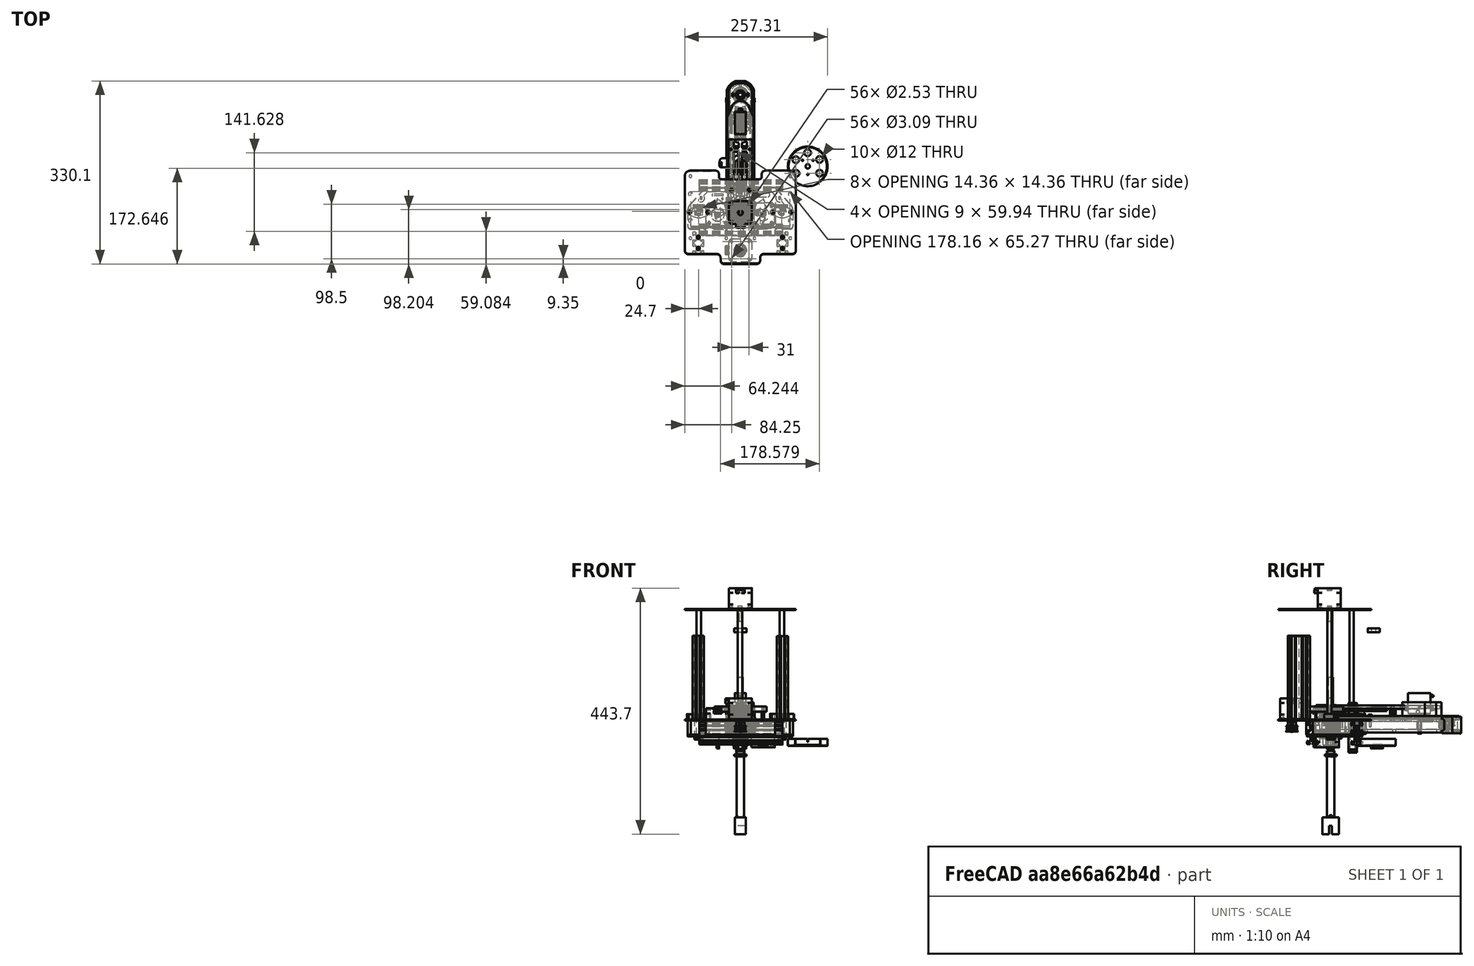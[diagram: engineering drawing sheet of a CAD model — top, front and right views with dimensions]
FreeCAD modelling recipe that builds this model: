
FCSTD DOCUMENT  (FreeCAD 1.0R38641 +468 (Git))
Label: zaxis
License: All rights reserved
LicenseURL: https://en.wikipedia.org/wiki/All_rights_reserved
objects: Part::Feature×117, Sketcher::SketchObject×42, App::Part×40, PartDesign::Body×25, PartDesign::Pad×24, PartDesign::Pocket×13, Mesh::Feature×12, TechDraw::DrawSVGTemplate×4, TechDraw::DrawPage×4, PartDesign::FeatureBase×2, PartDesign::Fillet×2, PartDesign::PolarPattern×1
note: 349 computed .brp shape members not serialized (recipe doc carries the construction recipe); baked Part::Feature solids carry a one-line shape summary decoded from their .brp

FEATURE [Sketcher::SketchObject] Sketch
  ArcFitTolerance = 1e-06
  AttachmentSupport = -> [XY_Plane001]
  FullyConstrained = false
  MakeInternals = false
  MapMode = 5
  sketch-geometry (70):
    g0: LineSegment StartX=-100 StartY=65.5055 StartZ=0 EndX=-100 EndY=-68.9082 EndZ=0
    g1: LineSegment StartX=100 StartY=-68.9082 StartZ=0 EndX=100 EndY=64.34 EndZ=0
    g2: GeomPoint [constr] X=0 Y=0 Z=0
    g3: LineSegment StartX=-93.9082 StartY=-75 StartZ=0 EndX=-42.611 EndY=-75 EndZ=0
    g4: LineSegment StartX=93.9082 StartY=-75 StartZ=0 EndX=42.611 EndY=-75 EndZ=0
    g5: LineSegment StartX=-35.5796 StartY=-82.0314 StartZ=0 EndX=-35.5796 EndY=-86.8204 EndZ=0
    g6: LineSegment StartX=-30.0002 StartY=-92.3998 StartZ=0 EndX=30.0002 EndY=-92.3998 EndZ=0
    g7: LineSegment StartX=35.5796 StartY=-86.8204 StartZ=0 EndX=35.5796 EndY=-82.0314 EndZ=0
    g8: LineSegment [constr] StartX=-127.885 StartY=50 StartZ=0 EndX=133.274 EndY=50 EndZ=0
    g9: LineSegment [constr] StartX=-138.289 StartY=-30 StartZ=0 EndX=153.891 EndY=-30 EndZ=0
    g10: LineSegment [constr] StartX=80 StartY=84.0683 StartZ=0 EndX=80 EndY=-102.927 EndZ=0
    g11: LineSegment [constr] StartX=-80 StartY=84.0683 StartZ=0 EndX=-80 EndY=-111.043 EndZ=0
    g12: ArcOfCircle CenterX=-93.9082 CenterY=-68.9082 CenterZ=0 NormalX=0 NormalY=0 NormalZ=1 AngleXU=0 Radius=6.09183 StartAngle=3.14159 EndAngle=4.71239
    g13: GeomPoint [constr] X=-100 Y=-75 Z=0
    g14: ArcOfCircle CenterX=-30.0002 CenterY=-86.8204 CenterZ=0 NormalX=0 NormalY=0 NormalZ=1 AngleXU=0 Radius=5.57938 StartAngle=3.14159 EndAngle=4.71239
    g15: GeomPoint [constr] X=-35.5796 Y=-92.3998 Z=0
    g16: ArcOfCircle CenterX=30.0002 CenterY=-86.8204 CenterZ=0 NormalX=0 NormalY=0 NormalZ=1 AngleXU=0 Radius=5.57938 StartAngle=4.71239 EndAngle=6.28319
    g17: GeomPoint [constr] X=35.5796 Y=-92.3998 Z=0
    g18: ArcOfCircle CenterX=-42.611 CenterY=-82.0314 CenterZ=0 NormalX=0 NormalY=0 NormalZ=1 AngleXU=0 Radius=7.03144 StartAngle=6e-16 EndAngle=1.5708
    g19: GeomPoint [constr] X=-35.5796 Y=-75 Z=0
    g20: ArcOfCircle CenterX=42.611 CenterY=-82.0314 CenterZ=0 NormalX=0 NormalY=0 NormalZ=1 AngleXU=0 Radius=7.03144 StartAngle=1.5708 EndAngle=3.14159
    g21: GeomPoint [constr] X=35.5796 Y=-75 Z=0
    g22: ArcOfCircle CenterX=93.9082 CenterY=-68.9082 CenterZ=0 NormalX=0 NormalY=0 NormalZ=1 AngleXU=0 Radius=6.09183 StartAngle=4.71239 EndAngle=6.28319
    g23: GeomPoint [constr] X=100 Y=-75 Z=0
    g24: LineSegment [constr] StartX=90 StartY=-14.05 StartZ=0 EndX=-90 EndY=-14.05 EndZ=0
    g25: LineSegment [constr] StartX=-90 StartY=-14.05 StartZ=0 EndX=-90 EndY=-45.95 EndZ=0
    g26: LineSegment [constr] StartX=-90 StartY=-45.95 StartZ=0 EndX=90 EndY=-45.95 EndZ=0
    g27: LineSegment [constr] StartX=90 StartY=-45.95 StartZ=0 EndX=90 EndY=-14.05 EndZ=0
    g28: LineSegment [constr] StartX=-90 StartY=65.95 StartZ=0 EndX=-90 EndY=34.05 EndZ=0
    g29: LineSegment [constr] StartX=-90 StartY=34.05 StartZ=0 EndX=90 EndY=34.05 EndZ=0
    g30: LineSegment [constr] StartX=90 StartY=34.05 StartZ=0 EndX=90 EndY=65.95 EndZ=0
    g31: LineSegment [constr] StartX=90 StartY=65.95 StartZ=0 EndX=-90 EndY=65.95 EndZ=0
    g32: Circle CenterX=90 CenterY=65.95 CenterZ=0 NormalX=0 NormalY=0 NormalZ=1 AngleXU=0 Radius=2.5
    g33: Circle CenterX=-90 CenterY=65.95 CenterZ=0 NormalX=0 NormalY=0 NormalZ=1 AngleXU=0 Radius=2.5
    g34: Circle CenterX=-90 CenterY=-45.95 CenterZ=0 NormalX=0 NormalY=0 NormalZ=1 AngleXU=0 Radius=2.5
    g35: Circle CenterX=90 CenterY=-45.95 CenterZ=0 NormalX=0 NormalY=0 NormalZ=1 AngleXU=0 Radius=2.5
    g36: LineSegment [constr] StartX=-76 StartY=-45 StartZ=0 EndX=-76 EndY=-65 EndZ=0
    g37: LineSegment [constr] StartX=-76 StartY=-65 StartZ=0 EndX=76 EndY=-65 EndZ=0
    g38: LineSegment [constr] StartX=76 StartY=-65 StartZ=0 EndX=76 EndY=-45 EndZ=0
    g39: LineSegment [constr] StartX=76 StartY=-45 StartZ=0 EndX=-76 EndY=-45 EndZ=0
    g40: GeomPoint [constr] X=-157.396 Y=0 Z=0
    g41: GeomPoint [constr] X=-25.3688 Y=-45.95 Z=0
    g42: GeomPoint [constr] X=25.3688 Y=-45.95 Z=0
    g43: Circle CenterX=-25.3688 CenterY=-45.95 CenterZ=0 NormalX=0 NormalY=0 NormalZ=1 AngleXU=0 Radius=2.5
    g44: Circle CenterX=25.3688 CenterY=-45.95 CenterZ=0 NormalX=0 NormalY=0 NormalZ=1 AngleXU=0 Radius=2.5
    g45: Circle CenterX=-90 CenterY=34.05 CenterZ=0 NormalX=0 NormalY=0 NormalZ=1 AngleXU=0 Radius=3.58
    g46: Circle CenterX=-90 CenterY=-14.05 CenterZ=0 NormalX=0 NormalY=0 NormalZ=1 AngleXU=0 Radius=3.58
    g47: Circle CenterX=90 CenterY=34.05 CenterZ=0 NormalX=0 NormalY=0 NormalZ=1 AngleXU=0 Radius=3.58
    g48: Circle CenterX=90 CenterY=-14.05 CenterZ=0 NormalX=0 NormalY=0 NormalZ=1 AngleXU=0 Radius=3.58
    g49: Circle CenterX=-76 CenterY=-65 CenterZ=0 NormalX=0 NormalY=0 NormalZ=1 AngleXU=0 Radius=2.7
    g50: Circle CenterX=-76 CenterY=-45 CenterZ=0 NormalX=0 NormalY=0 NormalZ=1 AngleXU=0 Radius=2.7
    g51: Circle CenterX=76 CenterY=-65 CenterZ=0 NormalX=0 NormalY=0 NormalZ=1 AngleXU=0 Radius=2.7
    g52: Circle CenterX=76 CenterY=-45 CenterZ=0 NormalX=0 NormalY=0 NormalZ=1 AngleXU=0 Radius=2.7
    g53: ArcOfCircle CenterX=89.2751 CenterY=64.34 CenterZ=0 NormalX=0 NormalY=0 NormalZ=1 AngleXU=0 Radius=10.7249 StartAngle=0 EndAngle=1.56696
    g54: GeomPoint [constr] X=100 Y=75 Z=0
    g55: ArcOfCircle CenterX=-90.4406 CenterY=65.5055 CenterZ=0 NormalX=0 NormalY=0 NormalZ=1 AngleXU=0 Radius=9.55939 StartAngle=1.5752 EndAngle=3.14159
    g56: GeomPoint [constr] X=-100 Y=75 Z=0
    g57: LineSegment StartX=-90.4827 StartY=75.0648 StartZ=0 EndX=-44.8342 EndY=75.0648 EndZ=0
    g58: LineSegment StartX=89.3163 StartY=75.0648 StartZ=0 EndX=44.8342 EndY=75.0648 EndZ=0
    g59: LineSegment StartX=38.4638 StartY=68.6944 StartZ=0 EndX=38.4638 EndY=63.8553 EndZ=0
    g60: LineSegment StartX=34.2439 StartY=59.6354 StartZ=0 EndX=-34.2439 EndY=59.6354 EndZ=0
    g61: LineSegment StartX=-38.4638 StartY=63.8553 StartZ=0 EndX=-38.4638 EndY=68.6944 EndZ=0
    g62: ArcOfCircle CenterX=-44.8342 CenterY=68.6944 CenterZ=0 NormalX=0 NormalY=0 NormalZ=1 AngleXU=0 Radius=6.37042 StartAngle=-9e-16 EndAngle=1.5708
    g63: GeomPoint [constr] X=-38.4638 Y=75.0648 Z=0
    g64: ArcOfCircle CenterX=44.8342 CenterY=68.6944 CenterZ=0 NormalX=0 NormalY=0 NormalZ=1 AngleXU=0 Radius=6.37042 StartAngle=1.5708 EndAngle=3.14159
    g65: GeomPoint [constr] X=38.4638 Y=75.0648 Z=0
    g66: ArcOfCircle CenterX=34.2439 CenterY=63.8553 CenterZ=0 NormalX=0 NormalY=0 NormalZ=1 AngleXU=0 Radius=4.21993 StartAngle=4.71239 EndAngle=6.28319
    g67: GeomPoint [constr] X=38.4638 Y=59.6354 Z=0
    g68: ArcOfCircle CenterX=-34.2439 CenterY=63.8553 CenterZ=0 NormalX=0 NormalY=0 NormalZ=1 AngleXU=0 Radius=4.21993 StartAngle=3.14159 EndAngle=4.71239
    g69: GeomPoint [constr] X=-38.4638 Y=59.6354 Z=0
  constraints (137):
    c: Vertical(g0)
    c: Vertical(g1)
    c: Horizontal(g3)
    c: Horizontal(g4)
    c: Vertical(g5)
    c: Horizontal(g6)
    c: Vertical(g7)
    c: Symmetric(g19,g21,g-2)
    c: Horizontal(g8)
    c: Horizontal(g9)
    c: DistanceY(g9,g8) = 80
    c: Vertical(g10)
    c: Vertical(g11)
    c: Symmetric(g11,g10,g-2)
    c: DistanceX(g13,g11) = 20
    c: DistanceX(g11,g10) = 160
    c: PointOnObject(g13,g0)
    c: PointOnObject(g13,g3)
    c: Tangent(g0,g12) = -1.5708
    c: Tangent(g3,g12) = -1.5708
    c: PointOnObject(g15,g5)
    c: PointOnObject(g15,g6)
    c: Tangent(g5,g14) = -1.5708
    c: Tangent(g6,g14) = -1.5708
    c: PointOnObject(g17,g6)
    c: PointOnObject(g17,g7)
    c: Tangent(g6,g16) = -1.5708
    c: Tangent(g7,g16) = -1.5708
    c: PointOnObject(g19,g3)
    c: PointOnObject(g19,g5)
    c: Tangent(g3,g18) = 1.5708
    c: Tangent(g5,g18) = 1.5708
    c: PointOnObject(g21,g4)
    c: PointOnObject(g21,g7)
    c: Tangent(g4,g20) = -1.5708
    c: Tangent(g7,g20) = 1.5708
    c: PointOnObject(g23,g1)
    c: PointOnObject(g23,g4)
    c: Tangent(g1,g22) = -1.5708
    c: Tangent(g4,g22) = 1.5708
    c: Horizontal(g12,g22)
    c: Coincident(g24,g25)
    c: Coincident(g25,g26)
    c: Coincident(g26,g27)
    c: Coincident(g27,g24)
    c: Horizontal(g24)
    c: Horizontal(g26)
    c: Vertical(g25)
    c: DistanceY(g26,g24) = 31.9
    c: Symmetric(g26,g24,g9)
    c: Coincident(g28,g29)
    c: Coincident(g29,g30)
    c: Coincident(g30,g31)
    c: Coincident(g31,g28)
    c: Vertical(g28)
    c: Horizontal(g29)
    c: Horizontal(g31)
    c: DistanceY(g29,g30) = 31.9
    c: Symmetric(g29,g30,g8)
    c: Vertical(g24,g29)
    c: Vertical(g28,g24)
    c: DistanceX(g56,g28) = 10
    c: DistanceX(g30,g54) = 10
    c: Coincident(g32,g30)
    c: Coincident(g33,g28)
    c: Coincident(g34,g25)
    c: Coincident(g35,g26)
    c: Equal(g35,g32)
    c: Equal(g35,g33)
    c: Equal(g35,g34)
    c: Coincident(g36,g37)
    c: Coincident(g37,g38)
    c: Coincident(g38,g39)
    c: Coincident(g39,g36)
    c: Vertical(g36)
    c: Vertical(g38)
    c: Horizontal(g39)
    c: DistanceY(g36,g36) = 20
    c: Symmetric(g36,g37,g-2)
    c: PointOnObject(g40,g-1)
    c: DistanceY(g36,g40) = 45
    c: DistanceX(g25,g36) = 14
    c: PointOnObject(g41,g26)
    c: Coincident(g43,g41)
    c: Coincident(g44,g42)
    c: Symmetric(g42,g41,g-2)
    c: Diameter(g34) = 5
    c: Diameter(g43) = 5
    c: Diameter(g44) = 5
    c: Coincident(g45,g28)
    c: Coincident(g46,g24)
    c: Coincident(g47,g29)
    c: Coincident(g48,g24)
    c: Equal(g47,g48)
    c: Equal(g47,g45)
    c: Equal(g47,g46)
    c: Diameter(g47) = 7.16
    c: Coincident(g49,g36)
    c: Coincident(g50,g36)
    c: Coincident(g51,g37)
    c: Coincident(g52,g38)
    c: Equal(g52,g51)
    c: Equal(g52,g49)
    c: Equal(g52,g50)
    c: Diameter(g52) = 5.4
    c: PointOnObject(g54,g1)
    c: Tangent(g1,g53) = -1.5708
    c: PointOnObject(g56,g0)
    c: Tangent(g0,g55) = -1.5708
    c: Coincident(g57,g55)
    c: Horizontal(g57)
    c: Coincident(g58,g53)
    c: Horizontal(g58)
    c: Vertical(g59)
    c: Horizontal(g60)
    c: Vertical(g61)
    c: Symmetric(g63,g65,g-2)
    c: PointOnObject(g63,g57)
    c: PointOnObject(g63,g61)
    c: Tangent(g57,g62) = 1.5708
    c: Tangent(g61,g62) = -1.5708
    c: PointOnObject(g65,g58)
    c: PointOnObject(g65,g59)
    c: Tangent(g58,g64) = -1.5708
    c: Tangent(g59,g64) = -1.5708
    c: PointOnObject(g67,g59)
    c: PointOnObject(g67,g60)
    c: Tangent(g59,g66) = 1.5708
    c: Tangent(g60,g66) = 1.5708
    c: PointOnObject(g69,g60)
    c: PointOnObject(g69,g61)
    c: Tangent(g60,g68) = 1.5708
    c: Tangent(g61,g68) = 1.5708
    c: Horizontal(g68,g66)
    c: Horizontal(g62,g64)
    c: Horizontal(g18,g20)
    c: Horizontal(g14,g16)
FEATURE [PartDesign::Pad] Pad
  Direction = (0,0,1)
  Length = 2
  Length2 = 10
  Profile = -> Sketch
  ReferenceAxis = -> Sketch [N_Axis]
  Refine = true
  Suppressed = false
  Type = 0
FEATURE [Mesh::Feature] Arm_Base_MotorPlate_1_1_003  label="Arm_Base_MotorPlate_1.1.003"
  Placement = pos=(0,0,113) rot=(0,0,1;0rad)
FEATURE [Mesh::Feature] Arm_Base_ZHub_Bottom_1_0_0  label="Arm_Base_ZHub_Bottom_1.0.0"
  Placement = pos=(25,30.5,141) rot=(0,0,1;3.14159rad)
FEATURE [Mesh::Feature] Arm_Base_ZHub_Top_1_0_0  label="Arm_Base_ZHub_Top_1.0.0"
  Placement = pos=(7.5,4.5e-15,112.5) rot=(1,0,0;3.14159rad)
FEATURE [Mesh::Feature] Arm_Shoulder_Connector_1_1_2  label="Arm_Shoulder_Connector_1.1.2"
  Placement = pos=(-3.6e-15,38,156) rot=(1,0,0;1.5708rad)
FEATURE [Mesh::Feature] Arm_Shoulder_Connector_1_1_003  label="Arm_Shoulder_Connector_1.1.003"
  Placement = pos=(0,38,85.5) rot=(1,0,0;1.5708rad)
FEATURE [Mesh::Feature] GT2_20_T_5mm_bore  label="GT2 20 T 5mm bore"
  Placement = pos=(-44,6,159) rot=(1,0,0;3.14159rad)
FEATURE [Mesh::Feature] GT2_20_T_5mm_bore001  label="GT2 20 T 5mm bore001"
  Placement = pos=(44,5.5,92) rot=(0,0,1;3.14159rad)
FEATURE [Part::Feature] Part__Feature003  label="LM8LUU Long Type Linear Bearing"
  Placement = pos=(-1.63e-14,39.5,31.8) rot=(0,1,0;1.5708rad)
  shape: bbox 15 x 15 x 45 mm, 34 faces (baked)
FEATURE [Part::Feature] Part__Feature005  label="LM8LUU Long Type Linear Bearing001"
  Placement = pos=(-6.4e-15,39.5,-12.8) rot=(0,1,0;1.5708rad)
  shape: bbox 15 x 15 x 45 mm, 34 faces (baked)
FEATURE [Part::Feature] Part__Feature008  label="p  BEARING, METRIC 600 MINIATURE SERIES, DOUBLE-SEALED  8mm ID × 22 OD × 7 W  —  608-2RS"
  Placement = pos=(-0.5,83.3,-46.6) rot=(0,0,1;0rad)
  shape: bbox 23.81 x 23.81 x 7.015 mm, 606 faces (baked)
FEATURE [Part::Feature] Part__Feature009  label="p  BEARING, METRIC 600 MINIATURE SERIES, DOUBLE-SEALED  8mm ID × 22 OD × 7 W  —  608-2RS001"
  Placement = pos=(0,77.5,163) rot=(0,0,1;0rad)
  shape: bbox 23.81 x 23.81 x 7.015 mm, 606 faces (baked)
FEATURE [Part::Feature] Part__Feature010  label="bearing"
  shape: bbox 8.659 x 4.3 x 8.659 mm, 17 faces (baked)
FEATURE [Part::Feature] Part__Feature011  label="bearing001"
  shape: bbox 8.659 x 4.3 x 8.659 mm, 17 faces (baked)
FEATURE [App::Part] bearing  label="bearing002"
  Group = -> [Part__Feature010,Part__Feature011]
  Origin = -> Origin005
FEATURE [Part::Feature] Part__Feature012  label="outer_plate"
  shape: bbox 12.9 x 8.6 x 12.9 mm, 12 faces (baked)
FEATURE [App::Part] GT2_Pulley_3mm_bore_v8  label="GT2 Pulley 3mm bore v8"
  Group = -> [bearing,Part__Feature012]
  Origin = -> Origin006
  Placement = pos=(44.8,29.9,9.8) rot=(1,0,0;1.5708rad)
FEATURE [Part::Feature] Part__Feature013  label="p  BEARING, SINGLE-ROW RADIAL, DOUBLE-SHIELDED, METRIC 6000-ZZ SERIES  —  6002-ZZ — 15mm ID × 32mm OD × 9mm W"
  shape: bbox 19.25 x 19.25 x 9 mm, 14 faces (baked)
FEATURE [Part::Feature] Part__Feature015  label="p  BEARING, SINGLE-ROW RADIAL, DOUBLE-SHIELDED, METRIC 6000-ZZ SERIES  —  6002-ZZ — 15mm ID × 32mm OD × 9mm W002"
  shape: bbox 29.3 x 29.3 x 8.937 mm, 1151 faces (baked)
FEATURE [Part::Feature] Part__Feature014  label="p  BEARING, SINGLE-ROW RADIAL, DOUBLE-SHIELDED, METRIC 6000-ZZ SERIES  —  6002-ZZ — 15mm ID × 32mm OD × 9mm W001"
  shape: bbox 34.64 x 34.64 x 9 mm, 14 faces (baked)
FEATURE [App::Part] p__BEARING__SINGLE_ROW_RADIAL__DOUBLE_SHIELDED__METRIC_6000_ZZ_SERIES_______6002_ZZ_____15mm_ID____32mm_OD____9mm_W  label="p  BEARING, SINGLE-ROW RADIAL, DOUBLE-SHIELDED, METRIC 6000-ZZ SERIES  —  6002-ZZ — 15mm ID × 32mm OD × 9mm W003"
  Group = -> [Part__Feature013,Part__Feature014,Part__Feature015]
  Origin = -> Origin007
  Placement = pos=(0,39.5,-33.1) rot=(0,0,1;0rad)
FEATURE [Part::Feature] Part__Feature016  label="p  BEARING, SINGLE-ROW RADIAL, DOUBLE-SHIELDED, METRIC 6000-ZZ SERIES  —  6002-ZZ — 15mm ID × 32mm OD × 9mm W004"
  shape: bbox 19.25 x 19.25 x 9 mm, 14 faces (baked)
FEATURE [Part::Feature] Part__Feature017  label="p  BEARING, SINGLE-ROW RADIAL, DOUBLE-SHIELDED, METRIC 6000-ZZ SERIES  —  6002-ZZ — 15mm ID × 32mm OD × 9mm W005"
  shape: bbox 34.64 x 34.64 x 9 mm, 14 faces (baked)
FEATURE [Part::Feature] Part__Feature018  label="p  BEARING, SINGLE-ROW RADIAL, DOUBLE-SHIELDED, METRIC 6000-ZZ SERIES  —  6002-ZZ — 15mm ID × 32mm OD × 9mm W006"
  shape: bbox 29.3 x 29.3 x 8.937 mm, 1151 faces (baked)
FEATURE [App::Part] p__BEARING__SINGLE_ROW_RADIAL__DOUBLE_SHIELDED__METRIC_6000_ZZ_SERIES_______6002_ZZ_____15mm_ID____32mm_OD____9mm_W001  label="p  BEARING, SINGLE-ROW RADIAL, DOUBLE-SHIELDED, METRIC 6000-ZZ SERIES  —  6002-ZZ — 15mm ID × 32mm OD × 9mm W007"
  Group = -> [Part__Feature016,Part__Feature017,Part__Feature018]
  Origin = -> Origin008
  Placement = pos=(0,39.5,9.5) rot=(0,0,1;0rad)
FEATURE [Part::Feature] Part__Feature019  label="KFL08Housing"
  shape: bbox 47 x 27 x 7.9 mm, 25 faces (baked)
FEATURE [Part::Feature] Part__Feature020  label="KFL08Bearing"
  shape: bbox 22 x 22 x 11.2 mm, 17 faces (baked)
FEATURE [Part::Feature] Part__Feature021  label="DIN_916-M3x3"
  Placement = pos=(0,-3.1,9.2) rot=(0,0,1;0rad)
  shape: bbox 3 x 3 x 3 mm, 11 faces (baked)
FEATURE [Part::Feature] Part__Feature022  label="DIN_916-M3x004"
  Placement = pos=(3.1,1.0252e-06,9.2) rot=(0,0,1;1.5708rad)
  shape: bbox 3 x 3 x 3 mm, 11 faces (baked)
FEATURE [App::Part] KFL08_Part  label="KFL08-Part"
  Group = -> [Part__Feature019,Part__Feature020,Part__Feature021,Part__Feature022]
  Origin = -> Origin009
  Placement = pos=(0,-2.5,2) rot=(0,0,1;0rad)
FEATURE [Part::Feature] Part__Feature024  label="Nema 17 model v004"
  Placement = pos=(1.48e-14,-70.5,40) rot=(0.707107,-0.707107,0;3.14159rad)
  shape: bbox 47.8 x 41.5 x 59.9 mm, 215 faces (baked)
FEATURE [Part::Feature] Part__Feature025  label="shf8mm"
  Placement = pos=(75,-2,2.5) rot=(0,0,1;3.14159rad)
  shape: bbox 43 x 24 x 10 mm, 66 faces (baked)
FEATURE [Part::Feature] Part__Feature026  label="Профиль V-slot 20x40"
  Placement = pos=(76,-33,-12.5) rot=(0.57735,-0.57735,-0.57735;2.0944rad)
  shape: bbox 150 x 20 x 40 mm, 80 faces (baked)
FEATURE [Part::Feature] Part__Feature027  label="Профиль V-slot 20x041"
  Placement = pos=(76,47,-13) rot=(0.57735,-0.57735,-0.57735;2.0944rad)
  shape: bbox 150 x 20 x 40 mm, 80 faces (baked)
FEATURE [Part::Feature] Part__Feature028  label="Профиль V-slot 20x042"
  Placement = pos=(76,-47.5,2.5) rot=(0,0,1;0rad)
  shape: bbox 20 x 40 x 150 mm, 80 faces (baked)
FEATURE [Part::Feature] Part__Feature029  label="Профиль V-slot 20x043"
  Placement = pos=(-76,-47.5,3) rot=(0,0,1;0rad)
  shape: bbox 20 x 40 x 150 mm, 80 faces (baked)
FEATURE [App::Part] Part003  label="RAIL"
  Group = -> [Part__Feature026,Part__Feature027]
  Origin = -> Origin011
  Placement = pos=(0,0,-2) rot=(0,0,1;0rad)
FEATURE [Sketcher::SketchObject] Sketch001
  ArcFitTolerance = 1e-06
  AttachmentSupport = -> [XY_Plane013]
  FullyConstrained = true
  MakeInternals = false
  MapMode = 5
  sketch-geometry (1):
    g0: Circle CenterX=0 CenterY=0 CenterZ=0 NormalX=0 NormalY=0 NormalZ=1 AngleXU=0 Radius=4
  constraints (2):
    c: Diameter(g0) = 8
    c: Coincident(g-1,g0)
FEATURE [PartDesign::Pad] Pad001
  Direction = (0,0,1)
  Length = 200
  Length2 = 10
  Profile = -> Sketch001
  ReferenceAxis = -> Sketch001 [N_Axis]
  Refine = true
  Suppressed = false
  Type = 0
FEATURE [PartDesign::Body] Body002  label="rod 8mm"
  AllowCompound = false
  Group = -> [Sketch001,Pad001]
  Origin = -> Origin013
  Placement = pos=(75,-2.5,0) rot=(0,0,1;0rad)
  Tip = -> Pad001
FEATURE [Sketcher::SketchObject] Sketch002
  ArcFitTolerance = 1e-06
  AttachmentSupport = -> [XY_Plane014]
  FullyConstrained = true
  MakeInternals = false
  MapMode = 5
  sketch-geometry (1):
    g0: Circle CenterX=0 CenterY=0 CenterZ=0 NormalX=0 NormalY=0 NormalZ=1 AngleXU=0 Radius=4
  constraints (2):
    c: Diameter(g0) = 8
    c: Coincident(g-1,g0)
FEATURE [PartDesign::Pad] Pad002
  Direction = (0,0,1)
  Length = 200
  Length2 = 10
  Profile = -> Sketch002
  ReferenceAxis = -> Sketch002 [N_Axis]
  Refine = true
  Suppressed = false
  Type = 0
FEATURE [PartDesign::Body] Body003  label="rod 8mm001"
  AllowCompound = false
  Group = -> [Sketch002,Pad002]
  Origin = -> Origin014
  Placement = pos=(-75,-1.5,0) rot=(0,0,1;0rad)
  Tip = -> Pad002
FEATURE [Sketcher::SketchObject] Sketch003
  ArcFitTolerance = 1e-06
  AttachmentSupport = -> [XY_Plane015]
  FullyConstrained = true
  MakeInternals = false
  MapMode = 5
  sketch-geometry (1):
    g0: Circle CenterX=0 CenterY=0 CenterZ=0 NormalX=0 NormalY=0 NormalZ=1 AngleXU=0 Radius=4
  constraints (2):
    c: Diameter(g0) = 8
    c: Coincident(g-1,g0)
FEATURE [PartDesign::Pad] Pad003
  Direction = (0,0,1)
  Length = 200
  Length2 = 10
  Profile = -> Sketch003
  ReferenceAxis = -> Sketch003 [N_Axis]
  Refine = true
  Suppressed = false
  Type = 0
FEATURE [PartDesign::Body] Body004  label="rod 8mm002"
  AllowCompound = false
  Group = -> [Sketch003,Pad003]
  Origin = -> Origin015
  Placement = pos=(-0.5,37.5,0) rot=(0,0,1;0rad)
  Tip = -> Pad003
FEATURE [Sketcher::SketchObject] Sketch005
  ArcFitTolerance = 1e-06
  AttachmentSupport = -> [XY_Plane017]
  FullyConstrained = true
  MakeInternals = false
  MapMode = 5
  sketch-geometry (1):
    g0: Circle CenterX=0 CenterY=0 CenterZ=0 NormalX=0 NormalY=0 NormalZ=1 AngleXU=0 Radius=3
  constraints (2):
    c: Coincident(g0,g-1)
    c: Diameter(g0) = 6
FEATURE [PartDesign::Body] Body006  label="fastener001"
  AllowCompound = false
  Group = -> [Sketch005]
  Origin = -> Origin017
  Placement = pos=(91.5,-48,-10) rot=(0,0,1;0rad)
FEATURE [Part::Feature] Part__Feature032  label="GT2_30T_5_6"
  Placement = pos=(-2.4e-15,-70,-2) rot=(0,1,0;3.14159rad)
  shape: bbox 23.27 x 23.27 x 17.5 mm, 336 faces (baked)
FEATURE [Part::Feature] Part__Feature033  label="15mm-wheel v003"
  Placement = pos=(0,-3.2e-15,-14.5) rot=(1,0,0;4.71239rad)
  shape: bbox 15.23 x 15.23 x 8.8 mm, 6 faces (baked)
FEATURE [Sketcher::SketchObject] Sketch006
  ArcFitTolerance = 1e-06
  AttachmentSupport = -> [XY_Plane019]
  FullyConstrained = true
  MakeInternals = false
  MapMode = 5
  sketch-geometry (1):
    g0: Circle CenterX=0 CenterY=0 CenterZ=0 NormalX=0 NormalY=0 NormalZ=1 AngleXU=0 Radius=3
  constraints (2):
    c: Coincident(g0,g-1)
    c: Diameter(g0) = 6
FEATURE [PartDesign::Pad] Pad006
  Direction = (0,0,1)
  Length = 10
  Length2 = 10
  Profile = -> Sketch006
  ReferenceAxis = -> Sketch006 [N_Axis]
  Refine = true
  Suppressed = false
  Type = 0
FEATURE [PartDesign::Body] Body007  label="fastener002"
  AllowCompound = false
  Group = -> [Sketch006,Pad006]
  Origin = -> Origin019
  Placement = pos=(0,0,0) rot=(1,0,0;3.14159rad)
  Tip = -> Pad006
FEATURE [App::Part] Part005  label="WHEEL ASSY001"
  Group = -> [Part__Feature033,Body007]
  Origin = -> Origin020
  Placement = pos=(25.5,-48.5,0) rot=(0,0,1;0rad)
FEATURE [Part::Feature] Part__Feature034  label="15mm-wheel v004"
  Placement = pos=(0,-2e-16,-15.5) rot=(1,0,0;4.71239rad)
  shape: bbox 15.23 x 15.23 x 8.8 mm, 6 faces (baked)
FEATURE [Sketcher::SketchObject] Sketch007
  ArcFitTolerance = 1e-06
  AttachmentSupport = -> [XY_Plane021]
  FullyConstrained = true
  MakeInternals = false
  MapMode = 5
  sketch-geometry (1):
    g0: Circle CenterX=0 CenterY=0 CenterZ=0 NormalX=0 NormalY=0 NormalZ=1 AngleXU=0 Radius=3
  constraints (2):
    c: Coincident(g0,g-1)
    c: Diameter(g0) = 6
FEATURE [PartDesign::Pad] Pad007
  Direction = (0,0,1)
  Length = 10
  Length2 = 10
  Profile = -> Sketch007
  ReferenceAxis = -> Sketch007 [N_Axis]
  Refine = true
  Suppressed = false
  Type = 0
FEATURE [Part::Feature] Part__Feature035  label="15mm-wheel v005"
  Placement = pos=(0,-2e-16,-15.5) rot=(1,0,0;4.71239rad)
  shape: bbox 15.23 x 15.23 x 8.8 mm, 6 faces (baked)
FEATURE [Sketcher::SketchObject] Sketch008
  ArcFitTolerance = 1e-06
  AttachmentSupport = -> [XY_Plane023]
  FullyConstrained = true
  MakeInternals = false
  MapMode = 5
  sketch-geometry (1):
    g0: Circle CenterX=0 CenterY=0 CenterZ=0 NormalX=0 NormalY=0 NormalZ=1 AngleXU=0 Radius=3
  constraints (2):
    c: Coincident(g0,g-1)
    c: Diameter(g0) = 6
FEATURE [PartDesign::Pad] Pad008
  Direction = (0,0,1)
  Length = 10
  Length2 = 10
  Profile = -> Sketch008
  ReferenceAxis = -> Sketch008 [N_Axis]
  Refine = true
  Suppressed = false
  Type = 0
FEATURE [PartDesign::Body] Body009  label="fastener004"
  AllowCompound = false
  Group = -> [Sketch008,Pad008]
  Origin = -> Origin023
  Placement = pos=(0,0,-10) rot=(0,0,1;0rad)
  Tip = -> Pad008
FEATURE [App::Part] Part007  label="WHEEL ASSY003"
  Group = -> [Part__Feature035,Body009]
  Origin = -> Origin024
  Placement = pos=(-25,-49,1) rot=(0,0,1;0rad)
FEATURE [Part::Feature] Part__Feature036  label="15mm-wheel v006"
  Placement = pos=(0,-2e-16,-15.5) rot=(1,0,0;4.71239rad)
  shape: bbox 15.23 x 15.23 x 8.8 mm, 6 faces (baked)
FEATURE [Sketcher::SketchObject] Sketch009
  ArcFitTolerance = 1e-06
  AttachmentSupport = -> [XY_Plane025]
  FullyConstrained = true
  MakeInternals = false
  MapMode = 5
  sketch-geometry (1):
    g0: Circle CenterX=0 CenterY=0 CenterZ=0 NormalX=0 NormalY=0 NormalZ=1 AngleXU=0 Radius=3
  constraints (2):
    c: Coincident(g0,g-1)
    c: Diameter(g0) = 6
FEATURE [PartDesign::Pad] Pad009
  Direction = (0,0,1)
  Length = 10
  Length2 = 10
  Profile = -> Sketch009
  ReferenceAxis = -> Sketch009 [N_Axis]
  Refine = true
  Suppressed = false
  Type = 0
FEATURE [PartDesign::Body] Body010  label="fastener005"
  AllowCompound = false
  Group = -> [Sketch009,Pad009]
  Origin = -> Origin025
  Placement = pos=(0,0,-10) rot=(0,0,1;0rad)
  Tip = -> Pad009
FEATURE [App::Part] Part008  label="WHEEL ASSY004"
  Group = -> [Part__Feature036,Body010]
  Origin = -> Origin026
  Placement = pos=(-90,-48.5,1) rot=(0,0,1;0rad)
FEATURE [Part::Feature] Part__Feature037  label="15mm-wheel v007"
  Placement = pos=(0,-2e-16,-15.5) rot=(1,0,0;4.71239rad)
  shape: bbox 15.23 x 15.23 x 8.8 mm, 6 faces (baked)
FEATURE [Sketcher::SketchObject] Sketch010
  ArcFitTolerance = 1e-06
  AttachmentSupport = -> [XY_Plane027]
  FullyConstrained = true
  MakeInternals = false
  MapMode = 5
  sketch-geometry (1):
    g0: Circle CenterX=0 CenterY=0 CenterZ=0 NormalX=0 NormalY=0 NormalZ=1 AngleXU=0 Radius=3
  constraints (2):
    c: Coincident(g0,g-1)
    c: Diameter(g0) = 6
FEATURE [PartDesign::Pad] Pad010
  Direction = (0,0,1)
  Length = 10
  Length2 = 10
  Profile = -> Sketch010
  ReferenceAxis = -> Sketch010 [N_Axis]
  Refine = true
  Suppressed = false
  Type = 0
FEATURE [PartDesign::Body] Body011  label="fastener006"
  AllowCompound = false
  Group = -> [Sketch010,Pad010]
  Origin = -> Origin027
  Placement = pos=(0,0,-10) rot=(0,0,1;0rad)
  Tip = -> Pad010
FEATURE [App::Part] Part009  label="WHEEL ASSY005"
  Group = -> [Part__Feature037,Body011]
  Origin = -> Origin028
  Placement = pos=(-90,-16.5,1) rot=(0,0,1;0rad)
FEATURE [Part::Feature] Part__Feature039  label="15mm-wheel v009"
  Placement = pos=(0,-2e-16,-15.5) rot=(1,0,0;4.71239rad)
  shape: bbox 15.23 x 15.23 x 8.8 mm, 6 faces (baked)
FEATURE [Sketcher::SketchObject] Sketch012
  ArcFitTolerance = 1e-06
  AttachmentSupport = -> [XY_Plane031]
  FullyConstrained = true
  MakeInternals = false
  MapMode = 5
  sketch-geometry (1):
    g0: Circle CenterX=0 CenterY=0 CenterZ=0 NormalX=0 NormalY=0 NormalZ=1 AngleXU=0 Radius=3
  constraints (2):
    c: Coincident(g0,g-1)
    c: Diameter(g0) = 6
FEATURE [PartDesign::Pad] Pad012
  Direction = (0,0,1)
  Length = 10
  Length2 = 10
  Profile = -> Sketch012
  ReferenceAxis = -> Sketch012 [N_Axis]
  Refine = true
  Suppressed = false
  Type = 0
FEATURE [PartDesign::Body] Body013  label="fastener008"
  AllowCompound = false
  Group = -> [Sketch012,Pad012]
  Origin = -> Origin031
  Placement = pos=(0,0,-10) rot=(0,0,1;0rad)
  Tip = -> Pad012
FEATURE [App::Part] Part011  label="WHEEL ASSY007"
  Group = -> [Part__Feature039,Body013]
  Origin = -> Origin032
  Placement = pos=(-90,63.5,1) rot=(0,0,1;0rad)
FEATURE [Part::Feature] Part__Feature040  label="15mm-wheel v010"
  Placement = pos=(0,-2e-16,-15.5) rot=(1,0,0;4.71239rad)
  shape: bbox 15.23 x 15.23 x 8.8 mm, 6 faces (baked)
FEATURE [Sketcher::SketchObject] Sketch013
  ArcFitTolerance = 1e-06
  AttachmentSupport = -> [XY_Plane033]
  FullyConstrained = true
  MakeInternals = false
  MapMode = 5
  sketch-geometry (1):
    g0: Circle CenterX=0 CenterY=0 CenterZ=0 NormalX=0 NormalY=0 NormalZ=1 AngleXU=0 Radius=3
  constraints (2):
    c: Coincident(g0,g-1)
    c: Diameter(g0) = 6
FEATURE [PartDesign::Pad] Pad013
  Direction = (0,0,1)
  Length = 10
  Length2 = 10
  Profile = -> Sketch013
  ReferenceAxis = -> Sketch013 [N_Axis]
  Refine = true
  Suppressed = false
  Type = 0
FEATURE [PartDesign::Body] Body014  label="fastener009"
  AllowCompound = false
  Group = -> [Sketch013,Pad013]
  Origin = -> Origin033
  Placement = pos=(0,0,-10) rot=(0,0,1;0rad)
  Tip = -> Pad013
FEATURE [App::Part] Part012  label="WHEEL ASSY008"
  Group = -> [Part__Feature040,Body014]
  Origin = -> Origin034
  Placement = pos=(-90,31.5,1) rot=(0,0,1;0rad)
FEATURE [Part::Feature] Part__Feature041  label="Nema 17 model v005"
  Placement = pos=(-3.86e-14,-2.5,239.1) rot=(1,0,0;3.14159rad)
  shape: bbox 41.5 x 47.8 x 59.9 mm, 215 faces (baked)
FEATURE [Sketcher::SketchObject] Sketch014
  ArcFitTolerance = 1e-06
  AttachmentSupport = -> [XY_Plane035]
  FullyConstrained = true
  MakeInternals = false
  MapMode = 5
  sketch-geometry (1):
    g0: Circle CenterX=0 CenterY=0 CenterZ=0 NormalX=0 NormalY=0 NormalZ=1 AngleXU=0 Radius=4
  constraints (2):
    c: Diameter(g0) = 8
    c: Coincident(g-1,g0)
FEATURE [PartDesign::Pad] Pad014
  Direction = (0,0,1)
  Length = 200
  Length2 = 10
  Profile = -> Sketch014
  ReferenceAxis = -> Sketch014 [N_Axis]
  Refine = true
  Suppressed = false
  Type = 0
FEATURE [PartDesign::Body] Body015  label="rod 8mm003"
  AllowCompound = false
  Group = -> [Sketch014,Pad014]
  Origin = -> Origin035
  Placement = pos=(-0.5,-2.5,6.5) rot=(0,0,1;0rad)
  Tip = -> Pad014
FEATURE [Sketcher::SketchObject] Sketch015
  ArcFitTolerance = 1e-06
  FullyConstrained = true
  MakeInternals = false
  MapMode = 5
  Placement = pos=(0,0,0) rot=(1,0,0;3.14159rad)
FEATURE [PartDesign::Body] Body008  label="fastener003"
  AllowCompound = false
  Group = -> [Sketch007,Pad007,Sketch015]
  Origin = -> Origin021
  Placement = pos=(0,0,-10) rot=(0,0,1;0rad)
  Tip = -> Pad007
FEATURE [App::Part] Part006  label="WHEEL ASSY002"
  Group = -> [Part__Feature034,Body008]
  Origin = -> Origin022
  Placement = pos=(90.5,-48.5,1) rot=(0,0,1;0rad)
FEATURE [Part::Feature] Part__Feature042  label="shf8mm001"
  Placement = pos=(2.76e-14,37.5,2.5) rot=(0,0,1;3.14159rad)
  shape: bbox 43 x 24 x 10 mm, 66 faces (baked)
FEATURE [Part::Feature] Part__Feature043  label="shf8mm002"
  Placement = pos=(-75,-2,2) rot=(0,0,1;3.14159rad)
  shape: bbox 43 x 24 x 10 mm, 66 faces (baked)
FEATURE [Part::Feature] Part__Feature044  label="15mm-wheel v011"
  Placement = pos=(0,-3.2e-15,-14.5) rot=(1,0,0;4.71239rad)
  shape: bbox 15.23 x 15.23 x 8.8 mm, 6 faces (baked)
FEATURE [Sketcher::SketchObject] Sketch018
  ArcFitTolerance = 1e-06
  AttachmentSupport = -> [XY_Plane037]
  FullyConstrained = true
  MakeInternals = false
  MapMode = 5
  sketch-geometry (1):
    g0: Circle CenterX=0 CenterY=0 CenterZ=0 NormalX=0 NormalY=0 NormalZ=1 AngleXU=0 Radius=3
  constraints (2):
    c: Coincident(g0,g-1)
    c: Diameter(g0) = 6
FEATURE [PartDesign::Pad] Pad016
  Direction = (0,0,1)
  Length = 10
  Length2 = 10
  Profile = -> Sketch018
  ReferenceAxis = -> Sketch018 [N_Axis]
  Refine = true
  Suppressed = false
  Type = 0
FEATURE [PartDesign::Body] Body017  label="fastener010"
  AllowCompound = false
  Group = -> [Sketch018,Pad016]
  Origin = -> Origin037
  Placement = pos=(0,0,0) rot=(1,0,0;3.14159rad)
  Tip = -> Pad016
FEATURE [App::Part] Part013  label="WHEEL ASSY009"
  Group = -> [Part__Feature044,Body017]
  Origin = -> Origin038
  Placement = pos=(91.5,31.5,-0.5) rot=(0,0,1;0rad)
FEATURE [Part::Feature] Part__Feature045  label="15mm-wheel v012"
  Placement = pos=(0,-3.2e-15,-14.5) rot=(1,0,0;4.71239rad)
  shape: bbox 15.23 x 15.23 x 8.8 mm, 6 faces (baked)
FEATURE [Sketcher::SketchObject] Sketch019
  ArcFitTolerance = 1e-06
  AttachmentSupport = -> [XY_Plane039]
  FullyConstrained = true
  MakeInternals = false
  MapMode = 5
  sketch-geometry (1):
    g0: Circle CenterX=0 CenterY=0 CenterZ=0 NormalX=0 NormalY=0 NormalZ=1 AngleXU=0 Radius=3
  constraints (2):
    c: Coincident(g0,g-1)
    c: Diameter(g0) = 6
FEATURE [PartDesign::Pad] Pad017
  Direction = (0,0,1)
  Length = 10
  Length2 = 10
  Profile = -> Sketch019
  ReferenceAxis = -> Sketch019 [N_Axis]
  Refine = true
  Suppressed = false
  Type = 0
FEATURE [PartDesign::Body] Body018  label="fastener011"
  AllowCompound = false
  Group = -> [Sketch019,Pad017]
  Origin = -> Origin039
  Placement = pos=(0,0,0) rot=(1,0,0;3.14159rad)
  Tip = -> Pad017
FEATURE [App::Part] Part014  label="WHEEL ASSY010"
  Group = -> [Part__Feature045,Body018]
  Origin = -> Origin040
  Placement = pos=(90.5,63.5,0) rot=(0,0,1;0rad)
FEATURE [Sketcher::SketchObject] Sketch020
  ArcFitTolerance = 1e-06
  AttachmentSupport = -> [Pad]
  FullyConstrained = false
  MakeInternals = false
  MapMode = 5
  Placement = pos=(0,0,0) rot=(1,0,0;3.14159rad)
  sketch-geometry (30):
    g0: LineSegment [constr] StartX=-51.8599 StartY=68 StartZ=0 EndX=46.814 EndY=68 EndZ=0
    g1: LineSegment [constr] StartX=-15.5 StartY=83.5 StartZ=0 EndX=-15.5 EndY=52.5 EndZ=0
    g2: LineSegment [constr] StartX=-15.5 StartY=52.5 StartZ=0 EndX=15.5 EndY=52.5 EndZ=0
    g3: LineSegment [constr] StartX=15.5 StartY=52.5 StartZ=0 EndX=15.5 EndY=83.5 EndZ=0
    g4: LineSegment [constr] StartX=15.5 StartY=83.5 StartZ=0 EndX=-15.5 EndY=83.5 EndZ=0
    g5: GeomPoint [constr] X=0 Y=68 Z=0
    g6: LineSegment [constr] StartX=-35.6384 StartY=-40 StartZ=0 EndX=78.9584 EndY=-40 EndZ=0
    g7: Circle [constr] CenterX=0 CenterY=0 CenterZ=0 NormalX=0 NormalY=0 NormalZ=1 AngleXU=0 Radius=18
    g8: Circle [constr] CenterX=-75 CenterY=0 CenterZ=0 NormalX=0 NormalY=0 NormalZ=1 AngleXU=0 Radius=16
    g9: Circle [constr] CenterX=75 CenterY=0 CenterZ=0 NormalX=0 NormalY=0 NormalZ=1 AngleXU=0 Radius=16
    g10: Circle [constr] CenterX=0 CenterY=-40 CenterZ=0 NormalX=0 NormalY=0 NormalZ=1 AngleXU=0 Radius=16
    g11: Circle CenterX=-15.5 CenterY=83.5 CenterZ=0 NormalX=0 NormalY=0 NormalZ=1 AngleXU=0 Radius=1.6
    g12: Circle CenterX=15.5 CenterY=83.5 CenterZ=0 NormalX=0 NormalY=0 NormalZ=1 AngleXU=0 Radius=1.6
    g13: Circle CenterX=0 CenterY=68 CenterZ=0 NormalX=0 NormalY=0 NormalZ=1 AngleXU=0 Radius=11.5
    g14: Circle CenterX=-15.5 CenterY=52.5 CenterZ=0 NormalX=0 NormalY=0 NormalZ=1 AngleXU=0 Radius=1.6
    g15: Circle CenterX=15.5 CenterY=52.5 CenterZ=0 NormalX=0 NormalY=0 NormalZ=1 AngleXU=0 Radius=1.6
    g16: Circle CenterX=-91 CenterY=0 CenterZ=0 NormalX=0 NormalY=0 NormalZ=1 AngleXU=0 Radius=2.6
    g17: Circle CenterX=-59 CenterY=0 CenterZ=0 NormalX=0 NormalY=0 NormalZ=1 AngleXU=0 Radius=2.6
    g18: Circle CenterX=-18 CenterY=0 CenterZ=0 NormalX=0 NormalY=0 NormalZ=1 AngleXU=0 Radius=2.6
    g19: Circle CenterX=18 CenterY=0 CenterZ=0 NormalX=0 NormalY=0 NormalZ=1 AngleXU=0 Radius=2.6
    g20: Circle CenterX=59 CenterY=0 CenterZ=0 NormalX=0 NormalY=0 NormalZ=1 AngleXU=0 Radius=2.6
    g21: Circle CenterX=91 CenterY=0 CenterZ=0 NormalX=0 NormalY=0 NormalZ=1 AngleXU=0 Radius=2.6
    g22: Circle CenterX=16 CenterY=-40 CenterZ=0 NormalX=0 NormalY=0 NormalZ=1 AngleXU=0 Radius=2.6
    g23: Circle CenterX=-16 CenterY=-40 CenterZ=0 NormalX=0 NormalY=0 NormalZ=1 AngleXU=0 Radius=2.6
    g24: LineSegment [constr] StartX=-54.8155 StartY=-14.7249 StartZ=0 EndX=-54.8155 EndY=-25.2784 EndZ=0
    g25: LineSegment [constr] StartX=-54.8155 StartY=-25.2784 StartZ=0 EndX=-32.26 EndY=-25.2784 EndZ=0
    g26: LineSegment [constr] StartX=-32.26 StartY=-25.2784 StartZ=0 EndX=-32.26 EndY=-14.7249 EndZ=0
    g27: LineSegment [constr] StartX=-32.26 StartY=-14.7249 StartZ=0 EndX=-54.8155 EndY=-14.7249 EndZ=0
    g28: Circle CenterX=-54.8155 CenterY=-14.7249 CenterZ=0 NormalX=0 NormalY=0 NormalZ=1 AngleXU=0 Radius=1.5
    g29: Circle CenterX=-32.26 CenterY=-25.2784 CenterZ=0 NormalX=0 NormalY=0 NormalZ=1 AngleXU=0 Radius=1.5
  constraints (72):
    c: Horizontal(g0)
    c: Coincident(g1,g2)
    c: Coincident(g2,g3)
    c: Coincident(g3,g4)
    c: Coincident(g4,g1)
    c: Vertical(g1)
    c: Vertical(g3)
    c: Horizontal(g2)
    c: Horizontal(g4)
    c: Symmetric(g3,g1,g5)
    c: PointOnObject(g5,g0)
    c: PointOnObject(g5,g-2)
    c: Horizontal(g6)
    c: Coincident(g7,g-1)
    c: PointOnObject(g8,g-1)
    c: PointOnObject(g10,g6)
    c: DistanceX(g1,g3) = 31
    c: DistanceY(g2,g3) = 31
    c: Coincident(g11,g1)
    c: Coincident(g12,g3)
    c: Coincident(g13,g5)
    c: Diameter(g13) = 23
    c: Coincident(g14,g1)
    c: Coincident(g15,g2)
    c: Equal(g11,g14)
    c: Equal(g11,g12)
    c: Equal(g11,g15)
    c: Diameter(g11) = 3.2
    c: DistanceY(g7,g0) = 68
    c: Equal(g8,g10)
    c: Equal(g8,g9)
    c: Diameter(g8) = 32
    c: PointOnObject(g16,g8)
    c: PointOnObject(g17,g8)
    c: PointOnObject(g18,g7)
    c: PointOnObject(g19,g7)
    c: PointOnObject(g20,g9)
    c: PointOnObject(g21,g9)
    c: PointOnObject(g22,g10)
    c: PointOnObject(g23,g10)
    c: Equal(g16, g17-g20) x4
    c: Equal(g16,g22)
    c: Equal(g16,g23)
    c: Equal(g16,g21)
    c: Diameter(g16) = 5.2
    c: PointOnObject(g17,g-1)
    c: PointOnObject(g16,g-1)
    c: PointOnObject(g18,g-1)
    c: PointOnObject(g19,g-1)
    c: PointOnObject(g20,g-1)
    c: PointOnObject(g21,g-1)
    c: PointOnObject(g22,g6)
    c: PointOnObject(g23,g6)
    c: PointOnObject(g10,g-2)
    c: DistanceX(g7,g9) = 75
    c: Symmetric(g8,g9,g-2)
    c: Diameter(g7) = 36
    c: DistanceY(g6,g7) = 40
    c: Coincident(g24,g25)
    c: Coincident(g25,g26)
    c: Coincident(g26,g27)
    c: Coincident(g27,g24)
    c: Vertical(g24)
    c: Vertical(g26)
    c: Horizontal(g25)
    c: Horizontal(g27)
    c: Block(g27)
    c: Block(g25)
    c: Coincident(g28,g24)
    c: Coincident(g29,g25)
    c: Equal(g28,g29)
    c: Diameter(g28) = 3
FEATURE [PartDesign::Pocket] Pocket
  BaseFeature = -> Pad
  Direction = (0,0,1)
  Length = 5
  Length2 = 5
  Profile = -> Sketch020
  ReferenceAxis = -> Sketch020 [N_Axis]
  Refine = true
  Suppressed = false
  Type = 1
FEATURE [Sketcher::SketchObject] Sketch021  label="nea17 zaxis pattern"
  ArcFitTolerance = 1e-06
  AttachmentSupport = -> [Pocket]
  FullyConstrained = true
  MakeInternals = false
  MapMode = 5
  Placement = pos=(0,0,0) rot=(1,0,0;3.14159rad)
  sketch-geometry (10):
    g0: Circle CenterX=0 CenterY=0 CenterZ=0 NormalX=0 NormalY=0 NormalZ=1 AngleXU=0 Radius=12.5
    g1: LineSegment [constr] StartX=15.5 StartY=15.5 StartZ=0 EndX=-15.5 EndY=15.5 EndZ=0
    g2: LineSegment [constr] StartX=-15.5 StartY=15.5 StartZ=0 EndX=-15.5 EndY=-15.5 EndZ=0
    g3: LineSegment [constr] StartX=-15.5 StartY=-15.5 StartZ=0 EndX=15.5 EndY=-15.5 EndZ=0
    g4: LineSegment [constr] StartX=15.5 StartY=-15.5 StartZ=0 EndX=15.5 EndY=15.5 EndZ=0
    g5: GeomPoint [constr] X=0 Y=0 Z=0
    g6: Circle CenterX=-15.5 CenterY=-15.5 CenterZ=0 NormalX=0 NormalY=0 NormalZ=1 AngleXU=0 Radius=1.6
    g7: Circle CenterX=15.5 CenterY=-15.5 CenterZ=0 NormalX=0 NormalY=0 NormalZ=1 AngleXU=0 Radius=1.6
    g8: Circle CenterX=15.5 CenterY=15.5 CenterZ=0 NormalX=0 NormalY=0 NormalZ=1 AngleXU=0 Radius=1.6
    g9: Circle CenterX=-15.5 CenterY=15.5 CenterZ=0 NormalX=0 NormalY=0 NormalZ=1 AngleXU=0 Radius=1.6
  constraints (22):
    c: Coincident(g0,g-1)
    c: Diameter(g0) = 25
    c: Coincident(g1,g2)
    c: Coincident(g2,g3)
    c: Coincident(g3,g4)
    c: Coincident(g4,g1)
    c: Horizontal(g1)
    c: Horizontal(g3)
    c: Vertical(g2)
    c: Vertical(g4)
    c: Symmetric(g3,g1,g5)
    c: Coincident(g5,g0)
    c: DistanceY(g3,g1) = 31
    c: DistanceX(g2,g3) = 31
    c: Coincident(g6,g2)
    c: Coincident(g7,g3)
    c: Coincident(g8,g1)
    c: Coincident(g9,g1)
    c: Equal(g9,g6)
    c: Equal(g9,g7)
    c: Equal(g9,g8)
    c: Diameter(g9) = 3.2
FEATURE [PartDesign::Body] Body  label="PLATES Z AXIS"
  AllowCompound = false
  Group = -> [Sketch,Pad,Sketch020,Pocket,Sketch021]
  Origin = -> Origin001
  Placement = pos=(0,-2.7,0) rot=(0,0,1;0rad)
  Tip = -> Pocket
FEATURE [Part::Feature] Part__Feature046  label="KW3-OZ"
  shape: bbox 5 x 5 x 5 mm, 6 faces (baked)
FEATURE [Part::Feature] Part__Feature047  label="KW3-OZ001"
  shape: bbox 40 x 27.99 x 10.1 mm, 639 faces (baked)
FEATURE [App::Part] KW3_OZ  label="KW3-OZ002"
  Group = -> [Part__Feature046,Part__Feature047]
  Origin = -> Origin041
  Placement = pos=(-43.5,17.5,-5) rot=(0,0,1;0rad)
FEATURE [Part::Feature] Part__Feature048  label="KW3-OZ004"
  shape: bbox 5 x 5 x 5 mm, 6 faces (baked)
FEATURE [Part::Feature] Part__Feature049  label="KW3-OZ005"
  shape: bbox 40 x 27.99 x 10.1 mm, 639 faces (baked)
FEATURE [App::Part] KW3_OZ001  label="KW3-OZ003"
  Group = -> [Part__Feature048,Part__Feature049]
  Origin = -> Origin042
  Placement = pos=(61,-64.5,118) rot=(0,-1,0;4.71239rad)
FEATURE [Mesh::Feature] Arm_Base_ZHub_Top_1_0_001  label="Arm_Base_ZHub_Top_1.0.001"
  Placement = pos=(-7.1,-2.4,28.8) rot=(0,0,1;3.14159rad)
FEATURE [Mesh::Feature] Arm_Base_MotorPlate_1_1_2  label="Arm_Base_MotorPlate_1.1.2"
  Placement = pos=(0,2.2,0) rot=(0,0,1;0rad)
FEATURE [App::Part] Part015  label="ZAXIS"
  Group = -> [Arm_Base_ZHub_Top_1_0_001,Arm_Base_MotorPlate_1_1_2]
  Origin = -> Origin043
FEATURE [Sketcher::SketchObject] Sketch022
  ArcFitTolerance = 1e-06
  AttachmentSupport = -> [XY_Plane044]
  FullyConstrained = false
  MakeInternals = false
  MapMode = 5
  sketch-geometry (27):
    g0: Circle CenterX=0 CenterY=0 CenterZ=0 NormalX=0 NormalY=0 NormalZ=1 AngleXU=0 Radius=7.5
    g1: LineSegment [constr] StartX=-27.5599 StartY=-40 StartZ=0 EndX=43.5599 EndY=-40 EndZ=0
    g2: LineSegment [constr] StartX=-51.7591 StartY=43 StartZ=0 EndX=60.4533 EndY=43 EndZ=0
    g3: Circle CenterX=0 CenterY=-40 CenterZ=0 NormalX=0 NormalY=0 NormalZ=1 AngleXU=0 Radius=5.25
    g4: Circle CenterX=0.0652184 CenterY=43 CenterZ=0 NormalX=0 NormalY=0 NormalZ=1 AngleXU=0 Radius=11
    g5: LineSegment StartX=17.4186 StartY=-21.7716 StartZ=0 EndX=15.72 EndY=32.896 EndZ=0
    g6: LineSegment StartX=-17.4186 StartY=-21.7716 StartZ=0 EndX=-15.72 EndY=33.0441 EndZ=0
    g7: LineSegment StartX=-4.33292 StartY=61.137 StartZ=0 EndX=4.33292 EndY=61.137 EndZ=0
    g8: LineSegment StartX=-18.2601 StartY=39.4677 StartZ=0 EndX=-18.2601 EndY=46.5323 EndZ=0
    g9: LineSegment StartX=18.3596 StartY=39.4677 StartZ=0 EndX=18.3596 EndY=46.5323 EndZ=0
    g10: ArcOfCircle CenterX=0.0652184 CenterY=43 CenterZ=0 NormalX=0 NormalY=0 NormalZ=1 AngleXU=0 Radius=18.6626 StartAngle=1.8087 EndAngle=2.95117
    g11: ArcOfCircle CenterX=0.0652184 CenterY=43 CenterZ=0 NormalX=0 NormalY=0 NormalZ=1 AngleXU=0 Radius=18.6323 StartAngle=0.190736 EndAngle=1.3397
    g12: ArcOfCircle CenterX=0.0652184 CenterY=43 CenterZ=0 NormalX=0 NormalY=0 NormalZ=1 AngleXU=0 Radius=18.6323 StartAngle=5.71003 EndAngle=6.09245
    g13: ArcOfCircle CenterX=0.0652184 CenterY=43 CenterZ=0 NormalX=0 NormalY=0 NormalZ=1 AngleXU=0 Radius=18.6626 StartAngle=3.33202 EndAngle=3.70429
    g14: LineSegment [constr] StartX=0 StartY=-40 StartZ=0 EndX=-21.7181 EndY=-61.7181 EndZ=0
    g15: LineSegment [constr] StartX=0 StartY=-40 StartZ=0 EndX=21.7181 EndY=-61.7181 EndZ=0
    g16: ArcOfCircle [constr] CenterX=0 CenterY=-40 CenterZ=0 NormalX=0 NormalY=0 NormalZ=1 AngleXU=0 Radius=30.714 StartAngle=3.92699 EndAngle=5.49779
    g17: LineSegment StartX=-17.4186 StartY=-52.4548 StartZ=0 EndX=-12.4548 EndY=-57.4186 EndZ=0
    g18: LineSegment StartX=17.4186 StartY=-52.8964 StartZ=0 EndX=12.8964 EndY=-57.4186 EndZ=0
    g19: LineSegment StartX=-12.4548 StartY=-57.4186 StartZ=0 EndX=12.8964 EndY=-57.4186 EndZ=0
    g20: LineSegment StartX=17.4186 StartY=-52.8964 StartZ=0 EndX=17.4186 EndY=-21.7716 EndZ=0
    g21: LineSegment StartX=-17.4186 StartY=-52.4548 StartZ=0 EndX=-17.4186 EndY=-21.7716 EndZ=0
    g22: Circle [constr] CenterX=0 CenterY=-40 CenterZ=0 NormalX=0 NormalY=0 NormalZ=1 AngleXU=0 Radius=8
    g23: Circle CenterX=0 CenterY=-32 CenterZ=0 NormalX=0 NormalY=0 NormalZ=1 AngleXU=0 Radius=1.6
    g24: Circle CenterX=8 CenterY=-40 CenterZ=0 NormalX=0 NormalY=0 NormalZ=1 AngleXU=0 Radius=1.6
    g25: Circle CenterX=0 CenterY=-48 CenterZ=0 NormalX=0 NormalY=0 NormalZ=1 AngleXU=0 Radius=1.6
    g26: Circle CenterX=-8 CenterY=-40 CenterZ=0 NormalX=0 NormalY=0 NormalZ=1 AngleXU=0 Radius=1.6
  constraints (60):
    c: Coincident(g0,g-1)
    c: Diameter(g0) = 15
    c: Horizontal(g1)
    c: Horizontal(g2)
    c: PointOnObject(g3,g1)
    c: Diameter(g3) = 10.5
    c: DistanceY(g1,g0) = 40
    c: DistanceY(g0,g2) = 43
    c: PointOnObject(g4,g2)
    c: Vertical(g9)
    c: Symmetric(g8,g8,g2)
    c: Equal(g9,g8)
    c: Coincident(g10,g4)
    c: Coincident(g10,g7)
    c: Coincident(g10,g8)
    c: Coincident(g11,g4)
    c: Coincident(g11,g7)
    c: Coincident(g11,g9)
    c: Coincident(g12,g4)
    c: Coincident(g12,g9)
    c: Coincident(g12,g5)
    c: Coincident(g13,g4)
    c: Coincident(g13,g8)
    c: Coincident(g13,g6)
    c: Diameter(g4) = 22
    c: Horizontal(g9,g8)
    c: PointOnObject(g3,g-2)
    c: Symmetric(g6,g5,g-2)
    c: Coincident(g14,g3)
    c: Coincident(g15,g3)
    c: Perpendicular(g15,g14)
    c: Angle(g15,g1) = 0.785398
    c: Coincident(g16,g3)
    c: Coincident(g16,g14)
    c: Coincident(g16,g15)
    c: Symmetric(g17,g17,g14)
    c: Symmetric(g18,g18,g15)
    c: Coincident(g19,g17)
    c: Coincident(g19,g18)
    c: Horizontal(g19)
    c: Symmetric(g7,g7,g-2)
    c: Coincident(g20,g18)
    c: Coincident(g21,g17)
    c: Coincident(g21,g6)
    c: Coincident(g20,g5)
    c: Parallel(g20,g21)
    c: Coincident(g22,g3)
    c: Diameter(g22) = 16
    c: PointOnObject(g23,g22)
    c: Symmetric(g1,g1,g24)
    c: PointOnObject(g25,g22)
    c: PointOnObject(g26,g1)
    c: Equal(g26,g25)
    c: Equal(g26,g24)
    c: Equal(g26,g23)
    c: Diameter(g26) = 3.2
    c: PointOnObject(g24,g22)
    c: PointOnObject(g23,g-2)
    c: PointOnObject(g26,g22)
    c: PointOnObject(g25,g-2)
FEATURE [PartDesign::Pad] Pad018
  Direction = (0,0,1)
  Length = 6
  Length2 = 10
  Profile = -> Sketch022
  ReferenceAxis = -> Sketch022 [N_Axis]
  Refine = true
  Suppressed = false
  Type = 0
FEATURE [Sketcher::SketchObject] Sketch004
  ArcFitTolerance = 1e-06
  FullyConstrained = true
  MakeInternals = false
  MapMode = 5
  Placement = pos=(-16.7279,0.518354,0) rot=(-0.565428,0.58322,0.58322;4.17081rad)
  sketch-geometry (1):
    g0: Circle CenterX=0 CenterY=3 CenterZ=0 NormalX=0 NormalY=0 NormalZ=1 AngleXU=0 Radius=1.4
  constraints (3):
    c: PointOnObject(g0,g-2)
    c: DistanceY(g-1,g0) = 3
    c: Diameter(g0) = 2.8
FEATURE [PartDesign::Pocket] Pocket002
  BaseFeature = -> Pad018
  Direction = (0.99952,-0.0309726,-1e-16)
  Length = 5
  Length2 = 5
  Profile = -> Sketch004
  ReferenceAxis = -> Sketch004 [N_Axis]
  Refine = true
  Suppressed = false
  Type = 1
FEATURE [Sketcher::SketchObject] Sketch024
  ArcFitTolerance = 1e-06
  AttachmentSupport = -> [Pocket002]
  ExternalGeometry = -> [Pocket002]
  FullyConstrained = false
  MakeInternals = false
  MapMode = 5
  Placement = pos=(-18.2601,0,0) rot=(0.57735,-0.57735,-0.57735;2.0944rad)
  sketch-geometry (2):
    g0: LineSegment [constr] StartX=-43 StartY=8.67581 StartZ=0 EndX=-43 EndY=3 EndZ=0
    g1: Circle CenterX=-43 CenterY=3 CenterZ=0 NormalX=0 NormalY=0 NormalZ=1 AngleXU=0 Radius=1.4
  constraints (4):
    c: Symmetric(g-3,g-3,g0)
    c: Coincident(g1,g0)
    c: Diameter(g1) = 2.8
    c: DistanceY(g0,g-3) = 3
FEATURE [PartDesign::Pocket] Pocket003
  BaseFeature = -> Pocket002
  Direction = (1,0,0)
  Length = 5
  Length2 = 5
  Profile = -> Sketch024
  ReferenceAxis = -> Sketch024 [N_Axis]
  Refine = true
  Suppressed = false
  Type = 1
FEATURE [Sketcher::SketchObject] Sketch025
  ArcFitTolerance = 1e-06
  AttachmentSupport = -> [Pocket003]
  FullyConstrained = true
  MakeInternals = false
  MapMode = 5
  Placement = pos=(0,61.137,0) rot=(0,0.707107,0.707107;3.14159rad)
  sketch-geometry (1):
    g0: Circle CenterX=0 CenterY=3 CenterZ=0 NormalX=0 NormalY=0 NormalZ=1 AngleXU=0 Radius=1.35
  constraints (3):
    c: PointOnObject(g0,g-2)
    c: DistanceY(g-1,g0) = 3
    c: Diameter(g0) = 2.7
FEATURE [PartDesign::Pocket] Pocket004
  BaseFeature = -> Pocket003
  Direction = (0,-1,2e-16)
  Length = 10
  Length2 = 5
  Profile = -> Sketch025
  ReferenceAxis = -> Sketch025 [N_Axis]
  Refine = true
  Suppressed = false
  Type = 0
FEATURE [Sketcher::SketchObject] Sketch026
  ArcFitTolerance = 1e-06
  AttachmentSupport = -> [XY_Plane045]
  FullyConstrained = false
  MakeInternals = false
  MapMode = 5
  sketch-geometry (90):
    g0: GeomPoint [constr] X=-75 Y=0 Z=0
    g1: GeomPoint [constr] X=75 Y=0 Z=0
    g2: GeomPoint [constr] X=0 Y=40 Z=0
    g3: LineSegment [constr] StartX=32.0408 StartY=29.5305 StartZ=0 EndX=49.7038 EndY=29.5305 EndZ=0
    g4: Circle CenterX=0 CenterY=40 CenterZ=0 NormalX=0 NormalY=0 NormalZ=1 AngleXU=0 Radius=7.6
    g5: Circle CenterX=-75 CenterY=0 CenterZ=0 NormalX=0 NormalY=0 NormalZ=1 AngleXU=0 Radius=7.6
    g6: Circle CenterX=75 CenterY=0 CenterZ=0 NormalX=0 NormalY=0 NormalZ=1 AngleXU=0 Radius=7.6
    g7: LineSegment StartX=95.1316 StartY=-0.265822 StartZ=0 EndX=95.1316 EndY=-25.433 EndZ=0
    g8: LineSegment StartX=-95.1316 StartY=-0.265822 StartZ=0 EndX=-95.1316 EndY=-25.4139 EndZ=0
    g9: ArcOfCircle CenterX=0 CenterY=40 CenterZ=0 NormalX=0 NormalY=0 NormalZ=1 AngleXU=0 Radius=13 StartAngle=0.232868 EndAngle=2.90872
    g10: LineSegment StartX=-61.029 StartY=43 StartZ=0 EndX=-12.6491 EndY=43 EndZ=0
    g11: LineSegment [constr] StartX=56.5 StartY=-21.7 StartZ=0 EndX=56.5 EndY=9.3 EndZ=0
    g12: LineSegment [constr] StartX=56.5 StartY=9.3 StartZ=0 EndX=25.5 EndY=9.3 EndZ=0
    g13: LineSegment [constr] StartX=25.5 StartY=9.3 StartZ=0 EndX=25.5 EndY=-21.7 EndZ=0
    g14: LineSegment [constr] StartX=25.5 StartY=-21.7 StartZ=0 EndX=56.5 EndY=-21.7 EndZ=0
    g15: GeomPoint [constr] X=41 Y=-6.2 Z=0
    g16: LineSegment StartX=-63 StartY=15.8 StartZ=0 EndX=-63 EndY=-28.2 EndZ=0
    g17: LineSegment StartX=-63 StartY=-28.2 StartZ=0 EndX=-19 EndY=-28.2 EndZ=0
    g18: LineSegment StartX=-19 StartY=-28.2 StartZ=0 EndX=-19 EndY=15.8 EndZ=0
    g19: LineSegment StartX=-19 StartY=15.8 StartZ=0 EndX=-63 EndY=15.8 EndZ=0
    g20: GeomPoint [constr] X=-41 Y=-6.2 Z=0
    g21: LineSegment StartX=61.029 StartY=43 StartZ=0 EndX=12.6491 EndY=43 EndZ=0
    g22: LineSegment StartX=89.9227 StartY=13.1961 StartZ=0 EndX=63.9873 EndY=41.6924 EndZ=0
    g23: LineSegment StartX=-89.9227 StartY=13.1961 StartZ=0 EndX=-63.9873 EndY=41.6924 EndZ=0
    g24: Circle CenterX=41 CenterY=-6.2 CenterZ=0 NormalX=0 NormalY=0 NormalZ=1 AngleXU=0 Radius=12.0573
    g25: ArcOfCircle CenterX=32.0408 CenterY=29.5305 CenterZ=0 NormalX=0 NormalY=0 NormalZ=1 AngleXU=0 Radius=1.55 StartAngle=1.5708 EndAngle=4.71239
    g26: ArcOfCircle CenterX=49.7038 CenterY=29.5305 CenterZ=0 NormalX=0 NormalY=0 NormalZ=1 AngleXU=0 Radius=1.55 StartAngle=4.71239 EndAngle=7.85398
    g27: LineSegment StartX=32.0408 StartY=31.0805 StartZ=0 EndX=49.7038 EndY=31.0805 EndZ=0
    g28: LineSegment StartX=32.0408 StartY=27.9805 StartZ=0 EndX=49.7038 EndY=27.9805 EndZ=0
    g29: ArcOfCircle CenterX=75.1316 CenterY=-0.265822 CenterZ=0 NormalX=0 NormalY=0 NormalZ=1 AngleXU=0 Radius=20 StartAngle=0 EndAngle=0.738387
    g30: GeomPoint [constr] X=95.1316 Y=7.47289 Z=0
    g31: ArcOfCircle CenterX=61.029 CenterY=39 CenterZ=0 NormalX=0 NormalY=0 NormalZ=1 AngleXU=0 Radius=4 StartAngle=0.738387 EndAngle=1.5708
    g32: GeomPoint [constr] X=62.7971 Y=43 Z=0
    g33: ArcOfCircle CenterX=89.1316 CenterY=-25.433 CenterZ=0 NormalX=0 NormalY=0 NormalZ=1 AngleXU=0 Radius=6 StartAngle=4.62873 EndAngle=6.28319
    g34: GeomPoint [constr] X=95.1316 Y=-33.2392 Z=0
    g35: ArcOfCircle CenterX=-89.1316 CenterY=-25.4139 CenterZ=0 NormalX=0 NormalY=0 NormalZ=1 AngleXU=0 Radius=6 StartAngle=3.14159 EndAngle=4.73736
    g36: GeomPoint [constr] X=-95.1316 Y=-33.2392 Z=0
    g37: ArcOfCircle CenterX=-75.1316 CenterY=-0.265822 CenterZ=0 NormalX=0 NormalY=0 NormalZ=1 AngleXU=0 Radius=20 StartAngle=2.40321 EndAngle=3.14159
    g38: GeomPoint [constr] X=-95.1316 Y=7.47289 Z=0
    g39: ArcOfCircle CenterX=-61.029 CenterY=39 CenterZ=0 NormalX=0 NormalY=0 NormalZ=1 AngleXU=0 Radius=4 StartAngle=1.5708 EndAngle=2.40321
    g40: GeomPoint [constr] X=-62.7971 Y=43 Z=0
    g41: Circle CenterX=0 CenterY=0 CenterZ=0 NormalX=0 NormalY=0 NormalZ=1 AngleXU=0 Radius=5.5
    g42: LineSegment StartX=-62.4394 StartY=-43 StartZ=0 EndX=62.4394 EndY=-43 EndZ=0
    g43: LineSegment StartX=88.6303 StartY=-31.412 StartZ=0 EndX=64.0188 EndY=-31.412 EndZ=0
    g44: LineSegment StartX=-88.9818 StartY=-31.412 StartZ=0 EndX=-64.8689 EndY=-31.412 EndZ=0
    g45: LineSegment StartX=-62.4394 StartY=-33.8415 StartZ=0 EndX=-62.4394 EndY=-43 EndZ=0
    g46: LineSegment StartX=62.4394 StartY=-43 StartZ=0 EndX=62.4394 EndY=-32.9914 EndZ=0
    g47: ArcOfCircle CenterX=-32.0408 CenterY=29.5305 CenterZ=0 NormalX=0 NormalY=0 NormalZ=1 AngleXU=0 Radius=3.5 StartAngle=4.71239 EndAngle=7.85398
    g48: ArcOfCircle CenterX=-49.7038 CenterY=29.5305 CenterZ=0 NormalX=0 NormalY=0 NormalZ=1 AngleXU=0 Radius=3.5 StartAngle=1.5708 EndAngle=4.71239
    g49: LineSegment StartX=-32.0408 StartY=26.0305 StartZ=0 EndX=-49.7038 EndY=26.0305 EndZ=0
    g50: LineSegment StartX=-32.0408 StartY=33.0305 StartZ=0 EndX=-49.7038 EndY=33.0305 EndZ=0
    g51: LineSegment [constr] StartX=-49.7038 StartY=29.5305 StartZ=0 EndX=-32.0408 EndY=29.5305 EndZ=0
    g52: LineSegment [constr] StartX=-25 StartY=-36 StartZ=0 EndX=25 EndY=-36 EndZ=0
    g53: Circle [constr] CenterX=0 CenterY=0 CenterZ=0 NormalX=0 NormalY=0 NormalZ=1 AngleXU=0 Radius=8
    g54: Circle CenterX=0 CenterY=8 CenterZ=0 NormalX=0 NormalY=0 NormalZ=1 AngleXU=0 Radius=1.5
    g55: Circle CenterX=0 CenterY=-8 CenterZ=0 NormalX=0 NormalY=0 NormalZ=1 AngleXU=0 Radius=1.5
    g56: Circle CenterX=8 CenterY=0 CenterZ=0 NormalX=0 NormalY=0 NormalZ=1 AngleXU=0 Radius=1.5
    g57: Circle CenterX=-8 CenterY=0 CenterZ=0 NormalX=0 NormalY=0 NormalZ=1 AngleXU=0 Radius=1.5
    g58: GeomPoint X=29.9135 Y=43 Z=0
    g59: GeomPoint X=104.419 Y=0 Z=0
    g60: LineSegment [constr] StartX=-75.6976 StartY=28.8258 StartZ=0 EndX=-70.9341 EndY=24.4904 EndZ=0
    g61: LineSegment [constr] StartX=-70.9341 StartY=24.4904 StartZ=0 EndX=70.9341 EndY=24.4904 EndZ=0
    g62: Circle CenterX=-70.9341 CenterY=24.4904 CenterZ=0 NormalX=0 NormalY=0 NormalZ=1 AngleXU=0 Radius=2.05
    g63: Circle CenterX=70.9341 CenterY=24.4904 CenterZ=0 NormalX=0 NormalY=0 NormalZ=1 AngleXU=0 Radius=2.05
    g64: Circle CenterX=25 CenterY=-36 CenterZ=0 NormalX=0 NormalY=0 NormalZ=1 AngleXU=0 Radius=2.05
    g65: Circle CenterX=-25 CenterY=-36 CenterZ=0 NormalX=0 NormalY=0 NormalZ=1 AngleXU=0 Radius=2.05
    g66: Circle CenterX=10 CenterY=19.2028 CenterZ=0 NormalX=0 NormalY=0 NormalZ=1 AngleXU=0 Radius=2
    g67: LineSegment [constr] StartX=10 StartY=19.2028 StartZ=0 EndX=-10 EndY=19.2028 EndZ=0
    g68: Circle CenterX=-10 CenterY=19.2028 CenterZ=0 NormalX=0 NormalY=0 NormalZ=1 AngleXU=0 Radius=2
    g69: LineSegment [constr] StartX=-73.3725 StartY=-21.7 StartZ=0 EndX=82.339 EndY=-21.7 EndZ=0
    g70: ArcOfCircle CenterX=-64.8689 CenterY=-33.8415 CenterZ=0 NormalX=0 NormalY=0 NormalZ=1 AngleXU=0 Radius=2.42951 StartAngle=-9e-16 EndAngle=1.5708
    g71: GeomPoint [constr] X=-62.4394 Y=-31.412 Z=0
    g72: ArcOfCircle CenterX=64.0188 CenterY=-32.9914 CenterZ=0 NormalX=0 NormalY=0 NormalZ=1 AngleXU=0 Radius=1.57941 StartAngle=1.5708 EndAngle=3.14159
    g73: GeomPoint [constr] X=62.4394 Y=-31.412 Z=0
    g74: ArcOfCircle CenterX=56.5 CenterY=9.3 CenterZ=0 NormalX=0 NormalY=0 NormalZ=1 AngleXU=0 Radius=1.55 StartAngle=3.14159 EndAngle=6.28319
    g75: ArcOfCircle CenterX=56.5 CenterY=11.3 CenterZ=0 NormalX=0 NormalY=0 NormalZ=1 AngleXU=0 Radius=1.55 StartAngle=0 EndAngle=3.14159
    g76: LineSegment StartX=54.95 StartY=9.3 StartZ=0 EndX=54.95 EndY=11.3 EndZ=0
    g77: LineSegment StartX=58.05 StartY=9.3 StartZ=0 EndX=58.05 EndY=11.3 EndZ=0
    g78: ArcOfCircle CenterX=25.5 CenterY=9.3 CenterZ=0 NormalX=0 NormalY=0 NormalZ=1 AngleXU=0 Radius=1.55 StartAngle=3.14159 EndAngle=6.28319
    g79: ArcOfCircle CenterX=25.5 CenterY=11.3 CenterZ=0 NormalX=0 NormalY=0 NormalZ=1 AngleXU=0 Radius=1.55 StartAngle=0 EndAngle=3.14159
    g80: LineSegment StartX=23.95 StartY=9.3 StartZ=0 EndX=23.95 EndY=11.3 EndZ=0
    g81: LineSegment StartX=27.05 StartY=9.3 StartZ=0 EndX=27.05 EndY=11.3 EndZ=0
    g82: ArcOfCircle CenterX=25.5 CenterY=-21.7 CenterZ=0 NormalX=0 NormalY=0 NormalZ=1 AngleXU=0 Radius=1.55 StartAngle=3.14159 EndAngle=6.28319
    g83: ArcOfCircle CenterX=25.5 CenterY=-19.7 CenterZ=0 NormalX=0 NormalY=0 NormalZ=1 AngleXU=0 Radius=1.55 StartAngle=9e-16 EndAngle=3.14159
    g84: LineSegment StartX=23.95 StartY=-21.7 StartZ=0 EndX=23.95 EndY=-19.7 EndZ=0
    g85: LineSegment StartX=27.05 StartY=-21.7 StartZ=0 EndX=27.05 EndY=-19.7 EndZ=0
    g86: ArcOfCircle CenterX=56.5 CenterY=-21.7 CenterZ=0 NormalX=0 NormalY=0 NormalZ=1 AngleXU=0 Radius=1.55 StartAngle=3.14159 EndAngle=6.28319
    g87: ArcOfCircle CenterX=56.5 CenterY=-19.7 CenterZ=0 NormalX=0 NormalY=0 NormalZ=1 AngleXU=0 Radius=1.55 StartAngle=-9e-16 EndAngle=3.14159
    g88: LineSegment StartX=54.95 StartY=-21.7 StartZ=0 EndX=54.95 EndY=-19.7 EndZ=0
    g89: LineSegment StartX=58.05 StartY=-21.7 StartZ=0 EndX=58.05 EndY=-19.7 EndZ=0
  constraints (192):
    c: PointOnObject(g0,g-1)
    c: PointOnObject(g2,g-2)
    c: Horizontal(g3)
    c: Symmetric(g0,g1,g-2)
    c: Coincident(g4,g2)
    c: Diameter(g4) = 15.2
    c: DistanceY(g-1,g2) = 40
    c: Coincident(g5,g0)
    c: Coincident(g6,g1)
    c: Equal(g6,g5)
    c: Diameter(g6) = 15.2
    c: DistanceX(g0,g1) = 150
    c: Vertical(g7)
    c: Vertical(g8)
    c: Symmetric(g34,g36,g-2)
    c: Coincident(g9,g2)
    c: Radius(g9) = 13
    c: Coincident(g9,g10)
    c: Coincident(g11,g12)
    c: Coincident(g12,g13)
    c: Coincident(g13,g14)
    c: Coincident(g14,g11)
    c: Vertical(g11)
    c: Vertical(g13)
    c: Horizontal(g12)
    c: Horizontal(g14)
    c: Symmetric(g13,g11,g15)
    c: Coincident(g16,g17)
    c: Coincident(g17,g18)
    c: Coincident(g18,g19)
    c: Coincident(g19,g16)
    c: Vertical(g16)
    c: Vertical(g18)
    c: Horizontal(g17)
    c: Horizontal(g19)
    c: Symmetric(g18,g16,g20)
    c: Symmetric(g15,g20,g-2)
    c: Horizontal(g21)
    c: Coincident(g21,g9)
    c: Horizontal(g9,g9)
    c: Symmetric(g40,g32,g-2)
    c: Horizontal(g38,g30)
    c: Distance(g12,g11) = 31
    c: Distance(g11,g11) = 31
    c: DistanceY(g17,g18) = 44
    c: DistanceX(g16,g18) = 44
    c: DistanceX(g20,g15) = 82
    c: Coincident(g24,g15)
    c: Tangent(g25,g27) = 1.5708
    c: Tangent(g25,g28) = -1.5708
    c: Tangent(g26,g27) = 1.5708
    c: Tangent(g26,g28) = -1.5708
    c: Equal(g25,g26)
    c: Diameter(g26) = 3.1
    c: PointOnObject(g30,g7)
    c: PointOnObject(g30,g22)
    c: Tangent(g7,g29) = 1.5708
    c: Tangent(g22,g29) = -1.5708
    c: PointOnObject(g32,g21)
    c: PointOnObject(g32,g22)
    c: Tangent(g21,g31) = -1.5708
    c: Tangent(g22,g31) = -1.5708
    c: PointOnObject(g34,g7)
    c: Tangent(g7,g33) = 1.5708
    c: PointOnObject(g36,g8)
    c: Tangent(g8,g35) = -1.5708
    c: PointOnObject(g38,g8)
    c: PointOnObject(g38,g23)
    c: Tangent(g8,g37) = -1.5708
    c: Tangent(g23,g37) = 1.5708
    c: PointOnObject(g40,g10)
    c: PointOnObject(g40,g23)
    c: Tangent(g10,g39) = 1.5708
    c: Tangent(g23,g39) = 1.5708
    c: Coincident(g41,g-1)
    c: Diameter(g41) = 11
    c: Coincident(g43,g33)
    c: Horizontal(g43)
    c: Coincident(g44,g35)
    c: Horizontal(g44)
    c: Vertical(g45)
    c: Coincident(g42,g45)
    c: Coincident(g46,g42)
    c: Vertical(g46)
    c: Symmetric(g42,g42,g-2)
    c: Horizontal(g71,g73)
    c: Tangent(g47,g49) = 1.5708
    c: Tangent(g47,g50) = -1.5708
    c: Tangent(g48,g49) = 1.5708
    c: Tangent(g48,g50) = -1.5708
    c: Equal(g47,g48)
    c: Horizontal(g50)
    c: Coincident(g51,g48)
    c: Coincident(g51,g47)
    c: Equal(g51,g3)
    c: Symmetric(g25,g47,g-2)
    c: Diameter(g47) = 7
    c: Coincident(g25,g3)
    c: Coincident(g3,g26)
    c: Coincident(g53,g41)
    c: Diameter(g53) = 16
    c: PointOnObject(g54,g53)
    c: PointOnObject(g55,g53)
    c: PointOnObject(g56,g53)
    c: PointOnObject(g57,g53)
    c: Equal(g57,g54)
    c: Equal(g57,g56)
    c: Equal(g57,g55)
    c: Diameter(g57) = 3
    c: PointOnObject(g54,g-2)
    c: PointOnObject(g57,g-1)
    c: PointOnObject(g55,g-2)
    c: PointOnObject(g56,g-1)
    c: PointOnObject(g58,g21)
    c: PointOnObject(g59,g-1)
    c: DistanceY(g59,g58) = 43
    c: DistanceY(g42,g59) = 43
    c: DistanceY(g52,g59) = 36
    c: Symmetric(g52,g52,g-2)
    c: DistanceX(g52,g52) = 50
    c: Equal(g35,g33)
    c: Radius(g35) = 6
    c: Equal(g29,g37)
    c: Radius(g29) = 20
    c: Equal(g39,g31)
    c: Radius(g39) = 4
    c: PointOnObject(g60,g23)
    c: Perpendicular(g23,g60)
    c: Coincident(g61,g60)
    c: Symmetric(g60,g61,g-2)
    c: Coincident(g62,g60)
    c: Coincident(g63,g61)
    c: Coincident(g64,g52)
    c: Coincident(g65,g52)
    c: Equal(g65,g64)
    c: Equal(g65,g63)
    c: Equal(g65,g62)
    c: Diameter(g65) = 4.1
    c: Diameter(g66) = 4
    c: Block(g3)
    c: Coincident(g67,g66)
    c: Diameter(g68) = 4
    c: Coincident(g67,g68)
    c: Symmetric(g67,g66,g-2)
    c: DistanceX(g67,g66) = 20
    c: DistanceY(g69,g59) = 21.7
    c: Horizontal(g69)
    c: PointOnObject(g13,g69)
    c: PointOnObject(g71,g44)
    c: PointOnObject(g71,g45)
    c: Tangent(g44,g70) = 1.5708
    c: Tangent(g45,g70) = 1.5708
    c: PointOnObject(g73,g43)
    c: PointOnObject(g73,g46)
    c: Tangent(g43,g72) = -1.5708
    c: Tangent(g46,g72) = 1.5708
    c: Tangent(g74,g76) = 1.5708
    c: Tangent(g74,g77) = -1.5708
    c: Tangent(g75,g76) = 1.5708
    c: Tangent(g75,g77) = -1.5708
    c: Equal(g74,g75)
    c: Coincident(g74,g11)
    c: PointOnObject(g75,g11)
    c: Diameter(g75) = 3.1
    c: DistanceY(g11,g75) = 2
    c: Tangent(g78,g80) = 1.5708
    c: Tangent(g78,g81) = -1.5708
    c: Tangent(g79,g80) = 1.5708
    c: Tangent(g79,g81) = -1.5708
    c: Equal(g78,g79)
    c: Coincident(g78,g12)
    c: Vertical(g80)
    c: Tangent(g82,g84) = 1.5708
    c: Tangent(g82,g85) = -1.5708
    c: Tangent(g83,g84) = 1.5708
    c: Tangent(g83,g85) = -1.5708
    c: Equal(g82,g83)
    c: Vertical(g85)
    c: Coincident(g82,g13)
    c: Tangent(g86,g88) = 1.5708
    c: Tangent(g86,g89) = -1.5708
    c: Tangent(g87,g88) = 1.5708
    c: Tangent(g87,g89) = -1.5708
    c: Equal(g86,g87)
    c: Vertical(g89)
    c: Coincident(g86,g11)
    c: DistanceY(g11,g87) = 2
    c: Horizontal(g83,g87)
    c: DistanceY(g12,g79) = 2
    c: Equal(g79,g83)
    c: Equal(g79,g87)
    c: Diameter(g79) = 3.1
FEATURE [Part::Feature] Part__Feature  label="NEMA17 42-40 v3"
  Placement = pos=(40.9,-6,1.3e-15) rot=(0,-0.707107,0.707107;3.14159rad)
  shape: bbox 42.02 x 47.1 x 72.37 mm, 266 faces (baked)
FEATURE [PartDesign::Pad] Pad019
  Direction = (0,0,1)
  Length = 3
  Length2 = 10
  Profile = -> Sketch026
  ReferenceAxis = -> Sketch026 [N_Axis]
  Refine = true
  Suppressed = false
  Type = 0
FEATURE [PartDesign::Body] Body020  label="motor plate metal 3mm"
  AllowCompound = false
  Group = -> [Sketch026,Pad019]
  Origin = -> Origin045
  Placement = pos=(0,0,1.5) rot=(0,0,1;0rad)
  Tip = -> Pad019
FEATURE [PartDesign::FeatureBase] Clone
  BaseFeature = -> Body020
  Suppressed = false
FEATURE [PartDesign::Body] Body021  label="Body004"
  AllowCompound = false
  Group = -> [Clone]
  Origin = -> Origin046
  Placement = pos=(-1.01e-14,0,-25) rot=(0,1,0;3.14159rad)
  Tip = -> Clone
FEATURE [Part::Feature] Part__Feature001  label="LM8LUU Long Type Linear Bearing002"
  Placement = pos=(-75.3,0,-34.2) rot=(0,1,0;4.71239rad)
  shape: bbox 15 x 15 x 45 mm, 34 faces (baked)
FEATURE [Part::Feature] Part__Feature050  label="NEMA17 42-40 v004"
  Placement = pos=(-40.7,-6.5,-25.6) rot=(1,0,0;1.5708rad)
  shape: bbox 42.02 x 47.1 x 72.37 mm, 266 faces (baked)
FEATURE [Part::Feature] Part__Feature051  label="LM8LUU Long Type Linear Bearing003"
  Placement = pos=(74.9,0,-34.2) rot=(0,1,0;4.71239rad)
  shape: bbox 15 x 15 x 45 mm, 34 faces (baked)
FEATURE [Part::Feature] Part__Feature052  label="NUT T8"
  Placement = pos=(0,0.1,-60.5) rot=(-1,0,0;3.14159rad)
  shape: bbox 22 x 22 x 15 mm, 20 faces (baked)
FEATURE [Part::Feature] Part__Feature053  label="GT2 Timing Pulley"
  Placement = pos=(8.36176,2.39887,15.0634) rot=(0,0,1;0rad)
  shape: bbox 16.24 x 16 x 16.24 mm, 198 faces (baked)
FEATURE [Part::Feature] Part__Feature054  label="M4 grub Screw"
  Placement = pos=(10.7618,6.20089,15.0634) rot=(0.447214,0.447214,-0.774597;1.82348rad)
  shape: bbox 5 x 4.758 x 5.494 mm, 36 faces (baked)
FEATURE [Part::Feature] Part__Feature055  label="M4 grub Screw001"
  Placement = pos=(8.36176,6.20089,12.6634) rot=(-0.186157,0.694747,-0.694747;2.77349rad)
  shape: bbox 5.494 x 4.758 x 5 mm, 36 faces (baked)
FEATURE [App::Part] GT2_Pulley_Assembly_With_Grub_Screws  label="GT2 Pulley Assembly With Grub Screws"
  Group = -> [Part__Feature053,Part__Feature054,Part__Feature055]
  Origin = -> Origin048
  Placement = pos=(-48.9,-21.5,-27.3) rot=(1,0,0;4.71239rad)
FEATURE [Part::Feature] Part__Feature056  label="GT2 Timing Pulley001"
  Placement = pos=(8.36176,2.39887,15.0634) rot=(0,0,1;0rad)
  shape: bbox 16.24 x 16 x 16.24 mm, 198 faces (baked)
FEATURE [Part::Feature] Part__Feature057  label="M4 grub Screw002"
  Placement = pos=(10.7618,6.20089,15.0634) rot=(0.447214,0.447214,-0.774597;1.82348rad)
  shape: bbox 5 x 4.758 x 5.494 mm, 36 faces (baked)
FEATURE [Part::Feature] Part__Feature058  label="M4 grub Screw003"
  Placement = pos=(8.36176,6.20089,12.6634) rot=(-0.186157,0.694747,-0.694747;2.77349rad)
  shape: bbox 5.494 x 4.758 x 5 mm, 36 faces (baked)
FEATURE [App::Part] GT2_Pulley_Assembly_With_Grub_Screws001  label="GT2 Pulley Assembly With Grub Screws001"
  Group = -> [Part__Feature056,Part__Feature057,Part__Feature058]
  Origin = -> Origin049
  Placement = pos=(32.4,-21,23.4) rot=(1,0,0;4.71239rad)
FEATURE [PartDesign::Body] Body023  label="ZAXIS THREAD SPACER UP"
  AllowCompound = false
  Origin = -> Origin051
FEATURE [Sketcher::SketchObject] Sketch027
  ArcFitTolerance = 1e-06
  AttachmentSupport = -> [XY_Plane054]
  FullyConstrained = false
  MakeInternals = false
  MapMode = 5
  sketch-geometry (80):
    g0: GeomPoint [constr] X=0 Y=40 Z=0
    g1: Circle CenterX=0 CenterY=40 CenterZ=0 NormalX=0 NormalY=0 NormalZ=1 AngleXU=0 Radius=7.6
    g2: LineSegment StartX=95.0792 StartY=-0.280145 StartZ=0 EndX=95.0792 EndY=-25.508 EndZ=0
    g3: LineSegment StartX=-95.0792 StartY=-0.280145 StartZ=0 EndX=-95.0792 EndY=-25.5006 EndZ=0
    g4: ArcOfCircle CenterX=0 CenterY=40 CenterZ=0 NormalX=0 NormalY=0 NormalZ=1 AngleXU=0 Radius=13 StartAngle=0.232868 EndAngle=2.90872
    g5: LineSegment StartX=-61.0532 StartY=43 StartZ=0 EndX=-12.6491 EndY=43 EndZ=0
    g6: LineSegment StartX=61.0532 StartY=43 StartZ=0 EndX=12.6491 EndY=43 EndZ=0
    g7: LineSegment StartX=89.8934 StartY=13.1563 StartZ=0 EndX=64.016 EndY=41.6873 EndZ=0
    g8: LineSegment StartX=-89.8934 StartY=13.1563 StartZ=0 EndX=-64.016 EndY=41.6873 EndZ=0
    g9: ArcOfCircle CenterX=75.0792 CenterY=-0.280145 CenterZ=0 NormalX=0 NormalY=0 NormalZ=1 AngleXU=0 Radius=20 StartAngle=0 EndAngle=0.736665
    g10: GeomPoint [constr] X=95.0792 Y=7.43877 Z=0
    g11: ArcOfCircle CenterX=61.0532 CenterY=39 CenterZ=0 NormalX=0 NormalY=0 NormalZ=1 AngleXU=0 Radius=4 StartAngle=0.736665 EndAngle=1.5708
    g12: GeomPoint [constr] X=62.8254 Y=43 Z=0
    g13: ArcOfCircle CenterX=89.0792 CenterY=-25.508 CenterZ=0 NormalX=0 NormalY=0 NormalZ=1 AngleXU=0 Radius=6 StartAngle=4.76414 EndAngle=6.28319
    g14: GeomPoint [constr] X=95.0792 Y=-33.2392 Z=0
    g15: ArcOfCircle CenterX=-89.0792 CenterY=-25.5006 CenterZ=0 NormalX=0 NormalY=0 NormalZ=1 AngleXU=0 Radius=6 StartAngle=3.14159 EndAngle=4.69778
    g16: GeomPoint [constr] X=-95.0792 Y=-33.2392 Z=0
    g17: ArcOfCircle CenterX=-75.0792 CenterY=-0.280145 CenterZ=0 NormalX=0 NormalY=0 NormalZ=1 AngleXU=0 Radius=20 StartAngle=2.40493 EndAngle=3.14159
    g18: GeomPoint [constr] X=-95.0792 Y=7.43877 Z=0
    g19: ArcOfCircle CenterX=-61.0532 CenterY=39 CenterZ=0 NormalX=0 NormalY=0 NormalZ=1 AngleXU=0 Radius=4 StartAngle=1.5708 EndAngle=2.40493
    g20: GeomPoint [constr] X=-62.8254 Y=43 Z=0
    g21: Circle CenterX=0 CenterY=0 CenterZ=0 NormalX=0 NormalY=0 NormalZ=1 AngleXU=0 Radius=5.5
    g22: LineSegment StartX=-62.444 StartY=-43 StartZ=0 EndX=62.444 EndY=-43 EndZ=0
    g23: LineSegment StartX=89.3896 StartY=-31.5 StartZ=0 EndX=64.0703 EndY=-31.5 EndZ=0
    g24: LineSegment StartX=-89.1669 StartY=-31.5 StartZ=0 EndX=-64.2169 EndY=-31.5 EndZ=0
    g25: LineSegment StartX=-62.444 StartY=-33.2729 StartZ=0 EndX=-62.444 EndY=-43 EndZ=0
    g26: LineSegment StartX=62.444 StartY=-43 StartZ=0 EndX=62.444 EndY=-33.1263 EndZ=0
    g27: LineSegment [constr] StartX=-25 StartY=-36 StartZ=0 EndX=25 EndY=-36 EndZ=0
    g28: Circle [constr] CenterX=0 CenterY=0 CenterZ=0 NormalX=0 NormalY=0 NormalZ=1 AngleXU=0 Radius=8
    g29: Circle CenterX=0 CenterY=8 CenterZ=0 NormalX=0 NormalY=0 NormalZ=1 AngleXU=0 Radius=1.5
    g30: Circle CenterX=0 CenterY=-8 CenterZ=0 NormalX=0 NormalY=0 NormalZ=1 AngleXU=0 Radius=1.5
    g31: Circle CenterX=8 CenterY=0 CenterZ=0 NormalX=0 NormalY=0 NormalZ=1 AngleXU=0 Radius=1.5
    g32: Circle CenterX=-8 CenterY=0 CenterZ=0 NormalX=0 NormalY=0 NormalZ=1 AngleXU=0 Radius=1.5
    g33: GeomPoint X=29.9135 Y=43 Z=0
    g34: GeomPoint X=104.419 Y=0 Z=0
    g35: LineSegment [constr] StartX=-75.6952 StartY=28.8105 StartZ=0 EndX=-70.9331 EndY=24.4913 EndZ=0
    g36: LineSegment [constr] StartX=-70.9331 StartY=24.4913 StartZ=0 EndX=70.9331 EndY=24.4913 EndZ=0
    g37: Circle CenterX=-70.9331 CenterY=24.4913 CenterZ=0 NormalX=0 NormalY=0 NormalZ=1 AngleXU=0 Radius=2.05
    g38: Circle CenterX=70.9331 CenterY=24.4913 CenterZ=0 NormalX=0 NormalY=0 NormalZ=1 AngleXU=0 Radius=2.05
    g39: Circle CenterX=25 CenterY=-36 CenterZ=0 NormalX=0 NormalY=0 NormalZ=1 AngleXU=0 Radius=2.05
    g40: Circle CenterX=-25 CenterY=-36 CenterZ=0 NormalX=0 NormalY=0 NormalZ=1 AngleXU=0 Radius=2.05
    g41: LineSegment StartX=-58.2414 StartY=36.7387 StartZ=0 EndX=-13.9414 EndY=36.7387 EndZ=0
    g42: LineSegment StartX=-10 StartY=11.7548 StartZ=0 EndX=10 EndY=11.7548 EndZ=0
    g43: LineSegment StartX=13.9414 StartY=36.7387 StartZ=0 EndX=54.8795 EndY=36.7387 EndZ=0
    g44: LineSegment StartX=74.5738 StartY=18.6005 StartZ=0 EndX=88.0801 EndY=3.70924 EndZ=0
    g45: LineSegment StartX=56.6253 StartY=35.9652 StartZ=0 EndX=64.5647 EndY=27.2116 EndZ=0
    g46: LineSegment StartX=89.0792 StartY=1.12057 StartZ=0 EndX=89.0792 EndY=-25.508 EndZ=0
    g47: LineSegment StartX=-89.0792 StartY=-25.5006 StartZ=0 EndX=-89.0792 EndY=-3.06717 EndZ=0
    g48: LineSegment StartX=-86.5706 StartY=3.43254 StartZ=0 EndX=-72.949 EndY=18.451 EndZ=0
    g49: LineSegment StartX=-59.6051 StartY=36.1345 StartZ=0 EndX=-66.2509 EndY=28.8072 EndZ=0
    g50: ArcOfCircle CenterX=-10 CenterY=19.3408 CenterZ=0 NormalX=0 NormalY=0 NormalZ=1 AngleXU=0 Radius=7.58607 StartAngle=1.71262 EndAngle=4.71239
    g51: ArcOfCircle CenterX=10 CenterY=19.3408 CenterZ=0 NormalX=0 NormalY=0 NormalZ=1 AngleXU=0 Radius=7.58607 StartAngle=4.71239 EndAngle=7.61744
    g52: LineSegment StartX=-11.0723 StartY=26.8507 StartZ=0 EndX=-13.9414 EndY=36.7387 EndZ=0
    g53: LineSegment StartX=13.9414 StartY=36.7387 StartZ=0 EndX=11.7777 EndY=26.7157 EndZ=0
    g54: LineSegment StartX=-89.0792 StartY=-25.5006 StartZ=0 EndX=-63.2159 EndY=-25.5006 EndZ=0
    g55: LineSegment StartX=-63.2159 StartY=-25.5006 StartZ=0 EndX=-63.2159 EndY=-28.53 EndZ=0
    g56: LineSegment StartX=-63.2159 StartY=-28.53 StartZ=0 EndX=63.2159 EndY=-28.53 EndZ=0
    g57: GeomPoint X=-49.3443 Y=0 Z=0
    g58: ArcOfCircle CenterX=-64.2169 CenterY=-33.2729 CenterZ=0 NormalX=0 NormalY=0 NormalZ=1 AngleXU=0 Radius=1.7729 StartAngle=1e-15 EndAngle=1.5708
    g59: GeomPoint [constr] X=-62.444 Y=-31.5 Z=0
    g60: ArcOfCircle CenterX=64.0703 CenterY=-33.1263 CenterZ=0 NormalX=0 NormalY=0 NormalZ=1 AngleXU=0 Radius=1.62635 StartAngle=1.5708 EndAngle=3.14159
    g61: GeomPoint [constr] X=62.444 Y=-31.5 Z=0
    g62: LineSegment StartX=89.0792 StartY=-25.508 StartZ=0 EndX=63.2159 EndY=-25.508 EndZ=0
    g63: LineSegment StartX=63.2159 StartY=-25.508 StartZ=0 EndX=63.2159 EndY=-28.53 EndZ=0
    g64: GeomPoint [constr] X=74.3916 Y=18.8014 Z=0
    g65: ArcOfCircle CenterX=85.226 CenterY=1.12057 CenterZ=0 NormalX=0 NormalY=0 NormalZ=1 AngleXU=0 Radius=3.85322 StartAngle=0 EndAngle=0.736665
    g66: GeomPoint [constr] X=89.0792 Y=2.6077 Z=0
    g67: ArcOfCircle CenterX=-79.4044 CenterY=-3.06717 CenterZ=0 NormalX=0 NormalY=0 NormalZ=1 AngleXU=0 Radius=9.67476 StartAngle=2.40493 EndAngle=3.14159
    g68: GeomPoint [constr] X=-89.0792 Y=0.666766 Z=0
    g69: GeomPoint [constr] X=-72.9918 Y=18.4039 Z=0
    g70: GeomPoint [constr] X=64.8592 Y=26.887 Z=0
    g71: ArcOfCircle CenterX=54.8795 CenterY=34.3818 CenterZ=0 NormalX=0 NormalY=0 NormalZ=1 AngleXU=0 Radius=2.35688 StartAngle=0.736665 EndAngle=1.5708
    g72: GeomPoint [constr] X=55.9237 Y=36.7387 Z=0
    g73: ArcOfCircle CenterX=-58.2414 CenterY=34.8977 CenterZ=0 NormalX=0 NormalY=0 NormalZ=1 AngleXU=0 Radius=1.84097 StartAngle=1.5708 EndAngle=2.40493
    g74: GeomPoint [constr] X=-59.0571 Y=36.7387 Z=0
    g75: GeomPoint [constr] X=-65.741 Y=29.3694 Z=0
    g76: Circle CenterX=10 CenterY=19.3408 CenterZ=0 NormalX=0 NormalY=0 NormalZ=1 AngleXU=0 Radius=2.15
    g77: Circle CenterX=-10 CenterY=19.3408 CenterZ=0 NormalX=0 NormalY=0 NormalZ=1 AngleXU=0 Radius=2.15
    g78: ArcOfCircle CenterX=70.9331 CenterY=24.4913 CenterZ=0 NormalX=0 NormalY=0 NormalZ=1 AngleXU=0 Radius=6.92504 StartAngle=2.7379 EndAngle=5.26596
    g79: ArcOfCircle CenterX=-70.9331 CenterY=24.4913 CenterZ=0 NormalX=0 NormalY=0 NormalZ=1 AngleXU=0 Radius=6.36785 StartAngle=4.39027 EndAngle=7.02789
  constraints (167):
    c: PointOnObject(g0,g-2)
    c: Coincident(g1,g0)
    c: Diameter(g1) = 15.2
    c: DistanceY(g-1,g0) = 40
    c: Vertical(g2)
    c: Vertical(g3)
    c: Symmetric(g14,g16,g-2)
    c: Coincident(g4,g0)
    c: Radius(g4) = 13
    c: Coincident(g4,g5)
    c: Horizontal(g6)
    c: Coincident(g6,g4)
    c: Horizontal(g4,g4)
    c: Symmetric(g20,g12,g-2)
    c: Horizontal(g18,g10)
    c: PointOnObject(g10,g2)
    c: PointOnObject(g10,g7)
    c: Tangent(g2,g9) = 1.5708
    c: Tangent(g7,g9) = -1.5708
    c: PointOnObject(g12,g6)
    c: PointOnObject(g12,g7)
    c: Tangent(g6,g11) = -1.5708
    c: Tangent(g7,g11) = -1.5708
    c: PointOnObject(g14,g2)
    c: Tangent(g2,g13) = 1.5708
    c: PointOnObject(g16,g3)
    c: Tangent(g3,g15) = -1.5708
    c: PointOnObject(g18,g3)
    c: PointOnObject(g18,g8)
    c: Tangent(g3,g17) = -1.5708
    c: Tangent(g8,g17) = 1.5708
    c: PointOnObject(g20,g5)
    c: PointOnObject(g20,g8)
    c: Tangent(g5,g19) = 1.5708
    c: Tangent(g8,g19) = 1.5708
    c: Coincident(g21,g-1)
    c: Diameter(g21) = 11
    c: Coincident(g23,g13)
    c: Horizontal(g23)
    c: Coincident(g24,g15)
    c: Horizontal(g24)
    c: Vertical(g25)
    c: Coincident(g22,g25)
    c: Coincident(g26,g22)
    c: Vertical(g26)
    c: Symmetric(g22,g22,g-2)
    c: Horizontal(g59,g61)
    c: Coincident(g28,g21)
    c: Diameter(g28) = 16
    c: PointOnObject(g29,g28)
    c: PointOnObject(g30,g28)
    c: PointOnObject(g31,g28)
    c: PointOnObject(g32,g28)
    c: Equal(g32,g29)
    c: Equal(g32,g31)
    c: Equal(g32,g30)
    c: Diameter(g32) = 3
    c: PointOnObject(g29,g-2)
    c: PointOnObject(g32,g-1)
    c: PointOnObject(g30,g-2)
    c: PointOnObject(g31,g-1)
    c: PointOnObject(g33,g6)
    c: PointOnObject(g34,g-1)
    c: DistanceY(g34,g33) = 43
    c: DistanceY(g22,g34) = 43
    c: DistanceY(g27,g34) = 36
    c: Symmetric(g27,g27,g-2)
    c: DistanceX(g27,g27) = 50
    c: Equal(g15,g13)
    c: Radius(g15) = 6
    c: Equal(g9,g17)
    c: Radius(g9) = 20
    c: Equal(g19,g11)
    c: Radius(g19) = 4
    c: PointOnObject(g35,g8)
    c: Perpendicular(g8,g35)
    c: Coincident(g36,g35)
    c: Symmetric(g35,g36,g-2)
    c: Coincident(g37,g35)
    c: Coincident(g38,g36)
    c: Coincident(g39,g27)
    c: Coincident(g40,g27)
    c: Equal(g40,g39)
    c: Equal(g40,g38)
    c: Equal(g40,g37)
    c: Diameter(g40) = 4.1
    c: Horizontal(g41)
    c: Horizontal(g42)
    c: Horizontal(g43)
    c: DistanceY(g13,g34) = 31.5
    c: Coincident(g46,g13)
    c: Parallel(g45,g7)
    c: Parallel(g44,g7)
    c: Vertical(g46)
    c: Coincident(g47,g15)
    c: Vertical(g47)
    c: Symmetric(g41,g43,g-2)
    c: Parallel(g48,g8)
    c: Parallel(g49,g8)
    c: Symmetric(g50,g51,g-2)
    c: DistanceX(g50,g51) = 20
    c: Tangent(g50,g42) = -1.5708
    c: Tangent(g51,g42) = -1.5708
    c: Coincident(g52,g50)
    c: Coincident(g52,g41)
    c: Coincident(g53,g43)
    c: Coincident(g53,g51)
    c: Coincident(g54,g15)
    c: Horizontal(g54)
    c: Coincident(g55,g54)
    c: Vertical(g55)
    c: Coincident(g56,g55)
    c: PointOnObject(g57,g-1)
    c: DistanceY(g55,g57) = 28.53
    c: PointOnObject(g59,g24)
    c: PointOnObject(g59,g25)
    c: Tangent(g24,g58) = 1.5708
    c: Tangent(g25,g58) = 1.5708
    c: PointOnObject(g61,g23)
    c: PointOnObject(g61,g26)
    c: Tangent(g23,g60) = -1.5708
    c: Tangent(g26,g60) = 1.5708
    c: Coincident(g62,g13)
    c: Horizontal(g62)
    c: Coincident(g63,g62)
    c: Coincident(g63,g56)
    c: Vertical(g63)
    c: Symmetric(g55,g56,g-2)
    c: PointOnObject(g64,g44)
    c: PointOnObject(g66,g44)
    c: PointOnObject(g66,g46)
    c: Tangent(g44,g65) = 1.5708
    c: Tangent(g46,g65) = 1.5708
    c: PointOnObject(g68,g47)
    c: PointOnObject(g68,g48)
    c: Tangent(g47,g67) = 1.5708
    c: Tangent(g48,g67) = 1.5708
    c: PointOnObject(g69,g48)
    c: PointOnObject(g70,g45)
    c: PointOnObject(g72,g43)
    c: PointOnObject(g72,g45)
    c: Tangent(g43,g71) = 1.5708
    c: Tangent(g45,g71) = 1.5708
    c: PointOnObject(g74,g41)
    c: PointOnObject(g74,g49)
    c: Tangent(g41,g73) = 1.5708
    c: Tangent(g49,g73) = -1.5708
    c: PointOnObject(g75,g49)
    c: Coincident(g76,g51)
    c: Coincident(g77,g50)
    c: Equal(g77,g76)
    c: Diameter(g77) = 4.3
    c: Block(g36)
    c: Coincident(g78,g36)
    c: Coincident(g78,g45)
    c: Coincident(g78,g44)
    c: Coincident(g79,g35)
    c: Coincident(g79,g49)
    c: Coincident(g79,g48)
    c: Block(g8)
    c: Block(g3)
    c: Block(g5)
    c: Block(g6)
    c: Block(g7)
    c: Block(g2)
    c: Block(g23)
    c: Block(g24)
FEATURE [PartDesign::Pad] Pad020
  Direction = (0,0,1)
  Length = 26
  Length2 = 10
  Profile = -> Sketch027
  ReferenceAxis = -> Sketch027 [N_Axis]
  Refine = true
  Suppressed = false
  Type = 0
FEATURE [Sketcher::SketchObject] Sketch028
  ArcFitTolerance = 1e-06
  AttachmentOffset = pos=(0,0,-4) rot=(0,0,1;0rad)
  AttachmentSupport = -> [Pad020]
  ExternalGeometry = -> [Pad020]
  FullyConstrained = false
  MakeInternals = false
  MapMode = 5
  Placement = pos=(0,0,22) rot=(0,0,1;0rad)
  sketch-geometry (8):
    g0: LineSegment StartX=-11.0734 StartY=47.3113 StartZ=0 EndX=-7.31133 EndY=51.0734 EndZ=0
    g1: LineSegment StartX=7.31133 StartY=51.0734 StartZ=0 EndX=11.0734 EndY=47.3113 EndZ=0
    g2: LineSegment [constr] StartX=0 StartY=40 StartZ=0 EndX=21.6985 EndY=61.6985 EndZ=0
    g3: LineSegment [constr] StartX=0 StartY=40 StartZ=0 EndX=-16.4017 EndY=56.4017 EndZ=0
    g4: LineSegment StartX=-7.31133 StartY=51.0734 StartZ=0 EndX=7.31133 EndY=51.0734 EndZ=0
    g5: LineSegment StartX=-11.0734 StartY=47.3113 StartZ=0 EndX=-9.26849 EndY=45.4643 EndZ=0
    g6: LineSegment StartX=11.0734 StartY=47.3113 StartZ=0 EndX=9.36927 EndY=45.2896 EndZ=0
    g7: ArcOfCircle CenterX=0 CenterY=40 CenterZ=0 NormalX=0 NormalY=0 NormalZ=1 AngleXU=0 Radius=10.7593 StartAngle=0.513959 EndAngle=2.60889
  constraints (16):
    c: Coincident(g2,g-3)
    c: Coincident(g3,g2)
    c: Perpendicular(g3,g2)
    c: Angle(g-2,g2) = 2.35619
    c: Symmetric(g0,g0,g3)
    c: Symmetric(g1,g1,g2)
    c: Tangent(g-3,g0)
    c: Tangent(g1,g-3)
    c: Coincident(g4,g0)
    c: Coincident(g4,g1)
    c: Horizontal(g4)
    c: Coincident(g5,g0)
    c: Coincident(g6,g1)
    c: Coincident(g7,g2)
    c: Coincident(g7,g5)
    c: Coincident(g7,g6)
FEATURE [PartDesign::Pad] Pad021
  BaseFeature = -> Pad020
  Direction = (0,0,1)
  Length = 18
  Length2 = 10
  Profile = -> Sketch028
  ReferenceAxis = -> Sketch028 [N_Axis]
  Refine = true
  Reversed = true
  Suppressed = false
  Type = 0
FEATURE [Sketcher::SketchObject] Sketch029
  ArcFitTolerance = 1e-06
  AttachmentSupport = -> [Pad021]
  FullyConstrained = true
  MakeInternals = false
  MapMode = 5
  Placement = pos=(29.1924,29.1924,0) rot=(0.281085,0.678598,0.678598;2.59356rad)
FEATURE [Sketcher::SketchObject] Sketch030
  ArcFitTolerance = 1e-06
  AttachmentSupport = -> [Pad021]
  FullyConstrained = true
  MakeInternals = false
  MapMode = 5
  Placement = pos=(29.1924,29.1924,0) rot=(0.281085,0.678598,0.678598;2.59356rad)
FEATURE [Sketcher::SketchObject] Sketch031
  ArcFitTolerance = 1e-06
  AttachmentSupport = -> [Pad021]
  ExternalGeometry = -> [Pad021]
  FullyConstrained = true
  MakeInternals = false
  MapMode = 5
  Placement = pos=(29.1924,29.1924,0) rot=(0.281085,0.678598,0.678598;2.59356rad)
  sketch-geometry (3):
    g0: Circle CenterX=28.2843 CenterY=18 CenterZ=0 NormalX=0 NormalY=0 NormalZ=1 AngleXU=0 Radius=1.25
    g1: Circle CenterX=28.2843 CenterY=8 CenterZ=0 NormalX=0 NormalY=0 NormalZ=1 AngleXU=0 Radius=1.25
    g2: LineSegment [constr] StartX=28.2843 StartY=18 StartZ=0 EndX=28.2843 EndY=8 EndZ=0
  constraints (7):
    c: Equal(g0,g1)
    c: Diameter(g0) = 2.5
    c: Coincident(g2,g0)
    c: Coincident(g2,g1)
    c: Symmetric(g-3,g-4,g2)
    c: DistanceY(g0,g-4) = 4
    c: DistanceY(g-4,g1) = 4
FEATURE [PartDesign::Pocket] Pocket005
  BaseFeature = -> Pad021
  Direction = (-0.707107,-0.707107,0)
  Length = 8
  Length2 = 5
  Profile = -> Sketch031
  ReferenceAxis = -> Sketch031 [N_Axis]
  Refine = true
  Suppressed = false
  Type = 0
FEATURE [Sketcher::SketchObject] Sketch032
  ArcFitTolerance = 1e-06
  AttachmentSupport = -> [Pocket005]
  ExternalGeometry = -> [Pocket005]
  FullyConstrained = true
  MakeInternals = false
  MapMode = 5
  Placement = pos=(-29.1924,29.1924,0) rot=(-0.281085,0.678598,0.678598;3.68962rad)
  sketch-geometry (3):
    g0: LineSegment [constr] StartX=-28.2843 StartY=18 StartZ=0 EndX=-28.2843 EndY=8 EndZ=0
    g1: Circle CenterX=-28.2843 CenterY=18 CenterZ=0 NormalX=0 NormalY=0 NormalZ=1 AngleXU=0 Radius=1.3
    g2: Circle CenterX=-28.2843 CenterY=8 CenterZ=0 NormalX=0 NormalY=0 NormalZ=1 AngleXU=0 Radius=1.3
  constraints (7):
    c: Symmetric(g-3,g-4,g0)
    c: DistanceY(g0,g-3) = 4
    c: DistanceY(g-3,g0) = 4
    c: Coincident(g1,g0)
    c: Coincident(g2,g0)
    c: Equal(g1,g2)
    c: Diameter(g1) = 2.6
FEATURE [PartDesign::Pocket] Pocket006
  BaseFeature = -> Pocket005
  Direction = (0.707107,-0.707107,2e-16)
  Length = 12
  Length2 = 5
  Profile = -> Sketch032
  ReferenceAxis = -> Sketch032 [N_Axis]
  Refine = true
  Suppressed = false
  Type = 0
FEATURE [PartDesign::Body] Body026  label="PLATES SPACER"
  AllowCompound = false
  Group = -> [Sketch027,Pad020,Sketch028,Pad021,Sketch029,Sketch030,Sketch031,Pocket005,Sketch032,Pocket006]
  Origin = -> Origin054
  Placement = pos=(0,-1,-25) rot=(0,0,1;0rad)
  Tip = -> Pocket006
FEATURE [Sketcher::SketchObject] Sketch033
  ArcFitTolerance = 1e-06
  AttachmentSupport = -> [XY_Plane055]
  FullyConstrained = true
  MakeInternals = false
  MapMode = 5
  sketch-geometry (1):
    g0: Circle CenterX=0 CenterY=0 CenterZ=0 NormalX=0 NormalY=0 NormalZ=1 AngleXU=0 Radius=14
  constraints (2):
    c: Coincident(g0,g-1)
    c: Diameter(g0) = 28
FEATURE [PartDesign::Pad] Pad022
  Direction = (0,0,1)
  Length = 16
  Length2 = 10
  Profile = -> Sketch033
  ReferenceAxis = -> Sketch033 [N_Axis]
  Refine = true
  Suppressed = false
  Type = 0
FEATURE [Sketcher::SketchObject] Sketch034
  ArcFitTolerance = 1e-06
  AttachmentSupport = -> [Pad022]
  FullyConstrained = false
  MakeInternals = false
  MapMode = 5
  Placement = pos=(0,0,16) rot=(0,0,1;0rad)
  sketch-geometry (7):
    g0: Circle CenterX=0 CenterY=0 CenterZ=0 NormalX=0 NormalY=0 NormalZ=1 AngleXU=0 Radius=5.5
    g1: Circle [constr] CenterX=0 CenterY=0 CenterZ=0 NormalX=0 NormalY=0 NormalZ=1 AngleXU=0 Radius=8
    g2: Circle CenterX=0 CenterY=-8 CenterZ=0 NormalX=0 NormalY=0 NormalZ=1 AngleXU=0 Radius=1.55
    g3: Circle CenterX=8 CenterY=0 CenterZ=0 NormalX=0 NormalY=0 NormalZ=1 AngleXU=0 Radius=1.55
    g4: Circle CenterX=0 CenterY=8 CenterZ=0 NormalX=0 NormalY=0 NormalZ=1 AngleXU=0 Radius=1.55
    g5: Circle CenterX=-7.99817 CenterY=0 CenterZ=0 NormalX=0 NormalY=0 NormalZ=1 AngleXU=0 Radius=1.2e-15
    g6: Circle CenterX=-7.99817 CenterY=0 CenterZ=0 NormalX=0 NormalY=0 NormalZ=1 AngleXU=0 Radius=1.55
  constraints (16):
    c: Coincident(g0,g-1)
    c: Diameter(g0) = 11
    c: Coincident(g1,g0)
    c: Diameter(g1) = 16
    c: PointOnObject(g2,g1)
    c: PointOnObject(g3,g1)
    c: PointOnObject(g4,g1)
    c: Coincident(g6,g5)
    c: Equal(g6,g2)
    c: Equal(g6,g3)
    c: Equal(g6,g4)
    c: Diameter(g6) = 3.1
    c: PointOnObject(g2,g-2)
    c: PointOnObject(g3,g-1)
    c: PointOnObject(g4,g-2)
    c: PointOnObject(g5,g-1)
FEATURE [PartDesign::Pocket] Pocket007
  BaseFeature = -> Pad022
  Direction = (0,0,-1)
  Length = 5
  Length2 = 5
  Profile = -> Sketch034
  ReferenceAxis = -> Sketch034 [N_Axis]
  Refine = true
  Suppressed = false
  Type = 1
FEATURE [PartDesign::Body] Body027  label="THREAD IDLER 1"
  AllowCompound = false
  Group = -> [Sketch033,Pad022,Sketch034,Pocket007]
  Origin = -> Origin055
  Placement = pos=(3.5e-15,0.4,-28.3) rot=(0,1,0;3.14159rad)
  Tip = -> Pocket007
FEATURE [Sketcher::SketchObject] Sketch035
  ArcFitTolerance = 1e-06
  AttachmentSupport = -> [XY_Plane056]
  FullyConstrained = true
  MakeInternals = false
  MapMode = 5
  sketch-geometry (1):
    g0: Circle CenterX=0 CenterY=0 CenterZ=0 NormalX=0 NormalY=0 NormalZ=1 AngleXU=0 Radius=14
  constraints (2):
    c: Coincident(g0,g-1)
    c: Diameter(g0) = 28
FEATURE [PartDesign::Pad] Pad023
  Direction = (0,0,1)
  Length = 12
  Length2 = 10
  Profile = -> Sketch035
  ReferenceAxis = -> Sketch035 [N_Axis]
  Refine = true
  Suppressed = false
  Type = 0
FEATURE [Sketcher::SketchObject] Sketch036
  ArcFitTolerance = 1e-06
  AttachmentSupport = -> [Pad023]
  FullyConstrained = false
  MakeInternals = false
  MapMode = 5
  Placement = pos=(0,0,12) rot=(0,0,1;0rad)
  sketch-geometry (7):
    g0: Circle CenterX=0 CenterY=0 CenterZ=0 NormalX=0 NormalY=0 NormalZ=1 AngleXU=0 Radius=5.5
    g1: Circle [constr] CenterX=0 CenterY=0 CenterZ=0 NormalX=0 NormalY=0 NormalZ=1 AngleXU=0 Radius=8
    g2: Circle CenterX=0 CenterY=-8 CenterZ=0 NormalX=0 NormalY=0 NormalZ=1 AngleXU=0 Radius=1.55
    g3: Circle CenterX=8 CenterY=0 CenterZ=0 NormalX=0 NormalY=0 NormalZ=1 AngleXU=0 Radius=1.55
    g4: Circle CenterX=0 CenterY=8 CenterZ=0 NormalX=0 NormalY=0 NormalZ=1 AngleXU=0 Radius=1.55
    g5: Circle CenterX=-7.99817 CenterY=0 CenterZ=0 NormalX=0 NormalY=0 NormalZ=1 AngleXU=0 Radius=1.2e-15
    g6: Circle CenterX=-7.99817 CenterY=0 CenterZ=0 NormalX=0 NormalY=0 NormalZ=1 AngleXU=0 Radius=1.55
  constraints (16):
    c: Coincident(g0,g-1)
    c: Diameter(g0) = 11
    c: Coincident(g1,g0)
    c: Diameter(g1) = 16
    c: PointOnObject(g2,g1)
    c: PointOnObject(g3,g1)
    c: PointOnObject(g4,g1)
    c: Coincident(g6,g5)
    c: Equal(g6,g2)
    c: Equal(g6,g3)
    c: Equal(g6,g4)
    c: Diameter(g6) = 3.1
    c: PointOnObject(g2,g-2)
    c: PointOnObject(g3,g-1)
    c: PointOnObject(g4,g-2)
    c: PointOnObject(g5,g-1)
FEATURE [PartDesign::Pocket] Pocket008
  BaseFeature = -> Pad023
  Direction = (0,0,-1)
  Length = 5
  Length2 = 5
  Profile = -> Sketch036
  ReferenceAxis = -> Sketch036 [N_Axis]
  Refine = true
  Suppressed = false
  Type = 1
FEATURE [PartDesign::Body] Body028  label="THREAD IDLER 002"
  AllowCompound = false
  Group = -> [Sketch035,Pad023,Sketch036,Pocket008]
  Origin = -> Origin056
  Placement = pos=(0.1,0.8,17.2) rot=(0,1,0;3.14159rad)
  Tip = -> Pocket008
FEATURE [Sketcher::SketchObject] Sketch037
  ArcFitTolerance = 1e-06
  AttachmentSupport = -> [XY_Plane057]
  FullyConstrained = false
  MakeInternals = false
  MapMode = 5
  sketch-geometry (50):
    g0: LineSegment StartX=-100 StartY=65.5055 StartZ=0 EndX=-100 EndY=-68.9082 EndZ=0
    g1: LineSegment StartX=100 StartY=-68.9082 StartZ=0 EndX=100 EndY=64.34 EndZ=0
    g2: LineSegment StartX=-93.9082 StartY=-75 StartZ=0 EndX=-42.611 EndY=-75 EndZ=0
    g3: LineSegment StartX=93.9082 StartY=-75 StartZ=0 EndX=42.611 EndY=-75 EndZ=0
    g4: LineSegment StartX=-35.5796 StartY=-82.0314 StartZ=0 EndX=-35.5796 EndY=-86.8204 EndZ=0
    g5: LineSegment StartX=-30.0002 StartY=-92.3998 StartZ=0 EndX=30.0002 EndY=-92.3998 EndZ=0
    g6: LineSegment StartX=35.5796 StartY=-86.8204 StartZ=0 EndX=35.5796 EndY=-82.0314 EndZ=0
    g7: LineSegment [constr] StartX=-127.885 StartY=50 StartZ=0 EndX=133.274 EndY=50 EndZ=0
    g8: LineSegment [constr] StartX=80 StartY=84.0683 StartZ=0 EndX=80 EndY=-102.927 EndZ=0
    g9: LineSegment [constr] StartX=-80 StartY=84.0683 StartZ=0 EndX=-80 EndY=-111.043 EndZ=0
    g10: ArcOfCircle CenterX=-93.9082 CenterY=-68.9082 CenterZ=0 NormalX=0 NormalY=0 NormalZ=1 AngleXU=0 Radius=6.09183 StartAngle=3.14159 EndAngle=4.71239
    g11: GeomPoint [constr] X=-100 Y=-75 Z=0
    g12: ArcOfCircle CenterX=-30.0002 CenterY=-86.8204 CenterZ=0 NormalX=0 NormalY=0 NormalZ=1 AngleXU=0 Radius=5.57938 StartAngle=3.14159 EndAngle=4.71239
    g13: GeomPoint [constr] X=-35.5796 Y=-92.3998 Z=0
    g14: ArcOfCircle CenterX=30.0002 CenterY=-86.8204 CenterZ=0 NormalX=0 NormalY=0 NormalZ=1 AngleXU=0 Radius=5.57938 StartAngle=4.71239 EndAngle=6.28319
    g15: GeomPoint [constr] X=35.5796 Y=-92.3998 Z=0
    g16: ArcOfCircle CenterX=-42.611 CenterY=-82.0314 CenterZ=0 NormalX=0 NormalY=0 NormalZ=1 AngleXU=0 Radius=7.03144 StartAngle=4e-16 EndAngle=1.5708
    g17: GeomPoint [constr] X=-35.5796 Y=-75 Z=0
    g18: ArcOfCircle CenterX=42.611 CenterY=-82.0314 CenterZ=0 NormalX=0 NormalY=0 NormalZ=1 AngleXU=0 Radius=7.03144 StartAngle=1.5708 EndAngle=3.14159
    g19: GeomPoint [constr] X=35.5796 Y=-75 Z=0
    g20: ArcOfCircle CenterX=93.9082 CenterY=-68.9082 CenterZ=0 NormalX=0 NormalY=0 NormalZ=1 AngleXU=0 Radius=6.09183 StartAngle=4.71239 EndAngle=6.28319
    g21: GeomPoint [constr] X=100 Y=-75 Z=0
    g22: LineSegment [constr] StartX=-76 StartY=-45 StartZ=0 EndX=-76 EndY=-65 EndZ=0
    g23: LineSegment [constr] StartX=-76 StartY=-65 StartZ=0 EndX=76 EndY=-65 EndZ=0
    g24: LineSegment [constr] StartX=76 StartY=-65 StartZ=0 EndX=76 EndY=-45 EndZ=0
    g25: LineSegment [constr] StartX=76 StartY=-45 StartZ=0 EndX=-76 EndY=-45 EndZ=0
    g26: GeomPoint [constr] X=-157.396 Y=0 Z=0
    g27: GeomPoint [constr] X=-25.3688 Y=-45.95 Z=0
    g28: GeomPoint [constr] X=25.3688 Y=-45.95 Z=0
    g29: Circle CenterX=-76 CenterY=-65 CenterZ=0 NormalX=0 NormalY=0 NormalZ=1 AngleXU=0 Radius=2.7
    g30: Circle CenterX=-76 CenterY=-45 CenterZ=0 NormalX=0 NormalY=0 NormalZ=1 AngleXU=0 Radius=2.7
    g31: Circle CenterX=76 CenterY=-65 CenterZ=0 NormalX=0 NormalY=0 NormalZ=1 AngleXU=0 Radius=2.7
    g32: Circle CenterX=76 CenterY=-45 CenterZ=0 NormalX=0 NormalY=0 NormalZ=1 AngleXU=0 Radius=2.7
    g33: ArcOfCircle CenterX=89.2751 CenterY=64.34 CenterZ=0 NormalX=0 NormalY=0 NormalZ=1 AngleXU=0 Radius=10.7249 StartAngle=0 EndAngle=1.56696
    g34: GeomPoint [constr] X=100 Y=75 Z=0
    g35: ArcOfCircle CenterX=-90.4406 CenterY=65.5055 CenterZ=0 NormalX=0 NormalY=0 NormalZ=1 AngleXU=0 Radius=9.55939 StartAngle=1.5752 EndAngle=3.14159
    g36: GeomPoint [constr] X=-100 Y=75 Z=0
    g37: LineSegment StartX=-90.4827 StartY=75.0648 StartZ=0 EndX=-44.8342 EndY=75.0648 EndZ=0
    g38: LineSegment StartX=89.3163 StartY=75.0648 StartZ=0 EndX=44.8342 EndY=75.0648 EndZ=0
    g39: LineSegment StartX=38.4638 StartY=68.6944 StartZ=0 EndX=38.4638 EndY=63.8553 EndZ=0
    g40: LineSegment StartX=34.2439 StartY=59.6354 StartZ=0 EndX=-34.2439 EndY=59.6354 EndZ=0
    g41: LineSegment StartX=-38.4638 StartY=63.8553 StartZ=0 EndX=-38.4638 EndY=68.6944 EndZ=0
    g42: ArcOfCircle CenterX=-44.8342 CenterY=68.6944 CenterZ=0 NormalX=0 NormalY=0 NormalZ=1 AngleXU=0 Radius=6.37042 StartAngle=-9e-16 EndAngle=1.5708
    g43: GeomPoint [constr] X=-38.4638 Y=75.0648 Z=0
    g44: ArcOfCircle CenterX=44.8342 CenterY=68.6944 CenterZ=0 NormalX=0 NormalY=0 NormalZ=1 AngleXU=0 Radius=6.37042 StartAngle=1.5708 EndAngle=3.14159
    g45: GeomPoint [constr] X=38.4638 Y=75.0648 Z=0
    g46: ArcOfCircle CenterX=34.2439 CenterY=63.8553 CenterZ=0 NormalX=0 NormalY=0 NormalZ=1 AngleXU=0 Radius=4.21993 StartAngle=4.71239 EndAngle=6.28319
    g47: GeomPoint [constr] X=38.4638 Y=59.6354 Z=0
    g48: ArcOfCircle CenterX=-34.2439 CenterY=63.8553 CenterZ=0 NormalX=0 NormalY=0 NormalZ=1 AngleXU=0 Radius=4.21993 StartAngle=3.14159 EndAngle=4.71239
    g49: GeomPoint [constr] X=-38.4638 Y=59.6354 Z=0
  constraints (91):
    c: Vertical(g0)
    c: Vertical(g1)
    c: Horizontal(g2)
    c: Horizontal(g3)
    c: Vertical(g4)
    c: Horizontal(g5)
    c: Vertical(g6)
    c: Symmetric(g17,g19,g-2)
    c: Horizontal(g7)
    c: Vertical(g8)
    c: Vertical(g9)
    c: Symmetric(g9,g8,g-2)
    c: DistanceX(g11,g9) = 20
    c: DistanceX(g9,g8) = 160
    c: PointOnObject(g11,g0)
    c: PointOnObject(g11,g2)
    c: Tangent(g0,g10) = -1.5708
    c: Tangent(g2,g10) = -1.5708
    c: PointOnObject(g13,g4)
    c: PointOnObject(g13,g5)
    c: Tangent(g4,g12) = -1.5708
    c: Tangent(g5,g12) = -1.5708
    c: PointOnObject(g15,g5)
    c: PointOnObject(g15,g6)
    c: Tangent(g5,g14) = -1.5708
    c: Tangent(g6,g14) = -1.5708
    c: PointOnObject(g17,g2)
    c: PointOnObject(g17,g4)
    c: Tangent(g2,g16) = 1.5708
    c: Tangent(g4,g16) = 1.5708
    c: PointOnObject(g19,g3)
    c: PointOnObject(g19,g6)
    c: Tangent(g3,g18) = -1.5708
    c: Tangent(g6,g18) = 1.5708
    c: PointOnObject(g21,g1)
    c: PointOnObject(g21,g3)
    c: Tangent(g1,g20) = -1.5708
    c: Tangent(g3,g20) = 1.5708
    c: Horizontal(g10,g20)
    c: Coincident(g22,g23)
    c: Coincident(g23,g24)
    c: Coincident(g24,g25)
    c: Coincident(g25,g22)
    c: Vertical(g22)
    c: Vertical(g24)
    c: Horizontal(g25)
    c: DistanceY(g22,g22) = 20
    c: Symmetric(g22,g23,g-2)
    c: PointOnObject(g26,g-1)
    c: DistanceY(g22,g26) = 45
    c: Symmetric(g28,g27,g-2)
    c: Coincident(g29,g22)
    c: Coincident(g30,g22)
    c: Coincident(g31,g23)
    c: Coincident(g32,g24)
    c: Equal(g32,g31)
    c: Equal(g32,g29)
    c: Equal(g32,g30)
    c: Diameter(g32) = 5.4
    c: PointOnObject(g34,g1)
    c: Tangent(g1,g33) = -1.5708
    c: PointOnObject(g36,g0)
    c: Tangent(g0,g35) = -1.5708
    c: Coincident(g37,g35)
    c: Horizontal(g37)
    c: Coincident(g38,g33)
    c: Horizontal(g38)
    c: Vertical(g39)
    c: Horizontal(g40)
    c: Vertical(g41)
    c: Symmetric(g43,g45,g-2)
    c: PointOnObject(g43,g37)
    c: PointOnObject(g43,g41)
    c: Tangent(g37,g42) = 1.5708
    c: Tangent(g41,g42) = -1.5708
    c: PointOnObject(g45,g38)
    c: PointOnObject(g45,g39)
    c: Tangent(g38,g44) = -1.5708
    c: Tangent(g39,g44) = -1.5708
    c: PointOnObject(g47,g39)
    c: PointOnObject(g47,g40)
    c: Tangent(g39,g46) = 1.5708
    c: Tangent(g40,g46) = 1.5708
    c: PointOnObject(g49,g40)
    c: PointOnObject(g49,g41)
    c: Tangent(g40,g48) = 1.5708
    c: Tangent(g41,g48) = 1.5708
    c: Horizontal(g48,g46)
    c: Horizontal(g42,g44)
    c: Horizontal(g16,g18)
    c: Horizontal(g12,g14)
FEATURE [PartDesign::Pad] Pad024
  Direction = (0,0,1)
  Length = 2
  Length2 = 10
  Profile = -> Sketch037
  ReferenceAxis = -> Sketch037 [N_Axis]
  Refine = true
  Suppressed = false
  Type = 0
FEATURE [Sketcher::SketchObject] Sketch038
  ArcFitTolerance = 1e-06
  AttachmentSupport = -> [Pad024]
  FullyConstrained = false
  MakeInternals = false
  MapMode = 5
  Placement = pos=(0,0,0) rot=(1,0,0;3.14159rad)
  sketch-geometry (10):
    g0: LineSegment [constr] StartX=-35.6384 StartY=-40 StartZ=0 EndX=78.9584 EndY=-40 EndZ=0
    g1: Circle [constr] CenterX=-75 CenterY=0 CenterZ=0 NormalX=0 NormalY=0 NormalZ=1 AngleXU=0 Radius=16
    g2: Circle [constr] CenterX=75 CenterY=0 CenterZ=0 NormalX=0 NormalY=0 NormalZ=1 AngleXU=0 Radius=16
    g3: Circle [constr] CenterX=0 CenterY=-40 CenterZ=0 NormalX=0 NormalY=0 NormalZ=1 AngleXU=0 Radius=16
    g4: Circle CenterX=-91 CenterY=0 CenterZ=0 NormalX=0 NormalY=0 NormalZ=1 AngleXU=0 Radius=2.6
    g5: Circle CenterX=-59 CenterY=0 CenterZ=0 NormalX=0 NormalY=0 NormalZ=1 AngleXU=0 Radius=2.6
    g6: Circle CenterX=59 CenterY=0 CenterZ=0 NormalX=0 NormalY=0 NormalZ=1 AngleXU=0 Radius=2.6
    g7: Circle CenterX=91 CenterY=0 CenterZ=0 NormalX=0 NormalY=0 NormalZ=1 AngleXU=0 Radius=2.6
    g8: Circle CenterX=16 CenterY=-40 CenterZ=0 NormalX=0 NormalY=0 NormalZ=1 AngleXU=0 Radius=2.6
    g9: Circle CenterX=-16 CenterY=-40 CenterZ=0 NormalX=0 NormalY=0 NormalZ=1 AngleXU=0 Radius=2.6
  constraints (26):
    c: Horizontal(g0)
    c: PointOnObject(g1,g-1)
    c: PointOnObject(g3,g0)
    c: Equal(g1,g3)
    c: Equal(g1,g2)
    c: Diameter(g1) = 32
    c: PointOnObject(g4,g1)
    c: PointOnObject(g5,g1)
    c: PointOnObject(g6,g2)
    c: PointOnObject(g7,g2)
    c: PointOnObject(g8,g3)
    c: PointOnObject(g9,g3)
    c: Equal(g4,g5)
    c: Equal(g4,g6)
    c: Equal(g4,g8)
    c: Equal(g4,g9)
    c: Equal(g4,g7)
    c: Diameter(g4) = 5.2
    c: PointOnObject(g5,g-1)
    c: PointOnObject(g4,g-1)
    c: PointOnObject(g6,g-1)
    c: PointOnObject(g7,g-1)
    c: PointOnObject(g8,g0)
    c: PointOnObject(g9,g0)
    c: PointOnObject(g3,g-2)
    c: Symmetric(g1,g2,g-2)
FEATURE [PartDesign::Pocket] Pocket009
  BaseFeature = -> Pad024
  Direction = (0,0,1)
  Length = 5
  Length2 = 5
  Profile = -> Sketch038
  ReferenceAxis = -> Sketch038 [N_Axis]
  Refine = true
  Suppressed = false
  Type = 1
FEATURE [Sketcher::SketchObject] Sketch039  label="nea17 zaxis pattern001"
  ArcFitTolerance = 1e-06
  AttachmentSupport = -> [Pocket009]
  FullyConstrained = true
  MakeInternals = false
  MapMode = 5
  Placement = pos=(0,0,0) rot=(1,0,0;3.14159rad)
  sketch-geometry (10):
    g0: Circle CenterX=0 CenterY=0 CenterZ=0 NormalX=0 NormalY=0 NormalZ=1 AngleXU=0 Radius=12.5
    g1: LineSegment [constr] StartX=15.5 StartY=15.5 StartZ=0 EndX=-15.5 EndY=15.5 EndZ=0
    g2: LineSegment [constr] StartX=-15.5 StartY=15.5 StartZ=0 EndX=-15.5 EndY=-15.5 EndZ=0
    g3: LineSegment [constr] StartX=-15.5 StartY=-15.5 StartZ=0 EndX=15.5 EndY=-15.5 EndZ=0
    g4: LineSegment [constr] StartX=15.5 StartY=-15.5 StartZ=0 EndX=15.5 EndY=15.5 EndZ=0
    g5: GeomPoint [constr] X=0 Y=0 Z=0
    g6: Circle CenterX=-15.5 CenterY=-15.5 CenterZ=0 NormalX=0 NormalY=0 NormalZ=1 AngleXU=0 Radius=1.6
    g7: Circle CenterX=15.5 CenterY=-15.5 CenterZ=0 NormalX=0 NormalY=0 NormalZ=1 AngleXU=0 Radius=1.6
    g8: Circle CenterX=15.5 CenterY=15.5 CenterZ=0 NormalX=0 NormalY=0 NormalZ=1 AngleXU=0 Radius=1.6
    g9: Circle CenterX=-15.5 CenterY=15.5 CenterZ=0 NormalX=0 NormalY=0 NormalZ=1 AngleXU=0 Radius=1.6
  constraints (22):
    c: Coincident(g0,g-1)
    c: Diameter(g0) = 25
    c: Coincident(g1,g2)
    c: Coincident(g2,g3)
    c: Coincident(g3,g4)
    c: Coincident(g4,g1)
    c: Horizontal(g1)
    c: Horizontal(g3)
    c: Vertical(g2)
    c: Vertical(g4)
    c: Symmetric(g3,g1,g5)
    c: Coincident(g5,g0)
    c: DistanceY(g3,g1) = 31
    c: DistanceX(g2,g3) = 31
    c: Coincident(g6,g2)
    c: Coincident(g7,g3)
    c: Coincident(g8,g1)
    c: Coincident(g9,g1)
    c: Equal(g9,g6)
    c: Equal(g9,g7)
    c: Equal(g9,g8)
    c: Diameter(g9) = 3.2
FEATURE [PartDesign::Pocket] Pocket010
  BaseFeature = -> Pocket009
  Direction = (0,0,1)
  Length = 5
  Length2 = 5
  Profile = -> Sketch039
  ReferenceAxis = -> Sketch039 [N_Axis]
  Refine = true
  Suppressed = false
  Type = 0
FEATURE [PartDesign::Body] Body029  label="PLATES Z AXIS001"
  AllowCompound = false
  Group = -> [Sketch037,Pad024,Sketch038,Pocket009,Sketch039,Pocket010]
  Origin = -> Origin057
  Placement = pos=(0,-1.8,199.8) rot=(0,0,1;0rad)
  Tip = -> Pocket010
FEATURE [App::Part] Part002  label="CARRIER ASSY"
  Group = -> [KFL08_Part,Body,Part__Feature024,Part__Feature025,Part__Feature028,Part__Feature029,Body002,Body003,Body004,Body006,Part__Feature032,Part005,Part006,Part007,Part008,Part009,Part011,Part012,Part__Feature041,Body015,Part__Feature042,Part__Feature043,Part013,Part014,KW3_OZ,KW3_OZ001,Body029]
  Origin = -> Origin010
FEATURE [TechDraw::DrawSVGTemplate] Template
  Height = 210
  Orientation = 1
  Template = /snap/freecad/1248/usr/share/Mod/TechDraw/Templates/Default_Template_A4_Landscape.svg
  Width = 297
FEATURE [TechDraw::DrawPage] Page
  KeepUpdated = true
  NextBalloonIndex = 1
  ProjectionType = 0
  Template = -> Template
FEATURE [TechDraw::DrawSVGTemplate] Template001
  Height = 210
  Orientation = 1
  Template = /snap/freecad/1248/usr/share/Mod/TechDraw/Templates/A4_Landscape_blank.svg
  Width = 297
FEATURE [TechDraw::DrawPage] Page001
  KeepUpdated = true
  NextBalloonIndex = 1
  ProjectionType = 0
  Template = -> Template001
FEATURE [TechDraw::DrawSVGTemplate] Template002
  EditableTexts = approval_person=B. Hecate; creator=A. Nemesis; date_of_issue=5/13/25; document_type=Assembly Drawing; general_tolerances=ISO 2768-m; identification_number=DN; language_code=EN; part_material=Stainless steel Mat.No. 1.4301; revision_index=AAA; sheet_number=3 / 3; sheet_scale=1 : 1; title=zaxis
  Height = 210
  Orientation = 1
  Template = /snap/freecad/1248/usr/share/Mod/TechDraw/Templates/A4_Landscape_ISO5457_minimal.svg
  Width = 297
FEATURE [TechDraw::DrawPage] Page002
  KeepUpdated = true
  NextBalloonIndex = 1
  ProjectionType = 0
  Template = -> Template002
FEATURE [TechDraw::DrawSVGTemplate] Template003
  Height = 210
  Orientation = 1
  Template = /snap/freecad/1248/usr/share/Mod/TechDraw/Templates/Default_Template_A4_Landscape.svg
  Width = 297
FEATURE [TechDraw::DrawPage] Page003
  KeepUpdated = true
  NextBalloonIndex = 1
  ProjectionType = 0
  Template = -> Template003
FEATURE [Mesh::Feature] Mesh001  label="motor plate metal 3mm (Meshed)"
FEATURE [Sketcher::SketchObject] Sketch181
  ArcFitTolerance = 1e-06
  AttachmentSupport = -> [XY_Plane062]
  FullyConstrained = false
  MakeInternals = false
  MapMode = 5
  sketch-geometry (2):
    g0: Circle CenterX=0 CenterY=0 CenterZ=0 NormalX=0 NormalY=0 NormalZ=1 AngleXU=0 Radius=35.8079
    g1: Circle CenterX=0 CenterY=0 CenterZ=0 NormalX=0 NormalY=0 NormalZ=1 AngleXU=0 Radius=4
  constraints (3):
    c: Coincident(g0,g-1)
    c: Coincident(g1,g0)
    c: Diameter(g1) = 8
FEATURE [PartDesign::Pad] Pad070
  Direction = (0,0,1)
  Length = 2
  Length2 = 10
  Profile = -> Sketch181
  ReferenceAxis = -> Sketch181 [N_Axis]
  Refine = true
  Suppressed = false
  Type = 0
FEATURE [Sketcher::SketchObject] Sketch182
  ArcFitTolerance = 1e-06
  AttachmentSupport = -> [Pad070]
  ExternalGeometry = -> [Pad070]
  FullyConstrained = true
  MakeInternals = false
  MapMode = 5
  Placement = pos=(0,0,0) rot=(1,0,0;3.14159rad)
  sketch-geometry (6):
    g0: ArcOfCircle CenterX=0 CenterY=0 CenterZ=0 NormalX=0 NormalY=0 NormalZ=1 AngleXU=0 Radius=35.8079 StartAngle=5.41052 EndAngle=10.2974
    g1: ArcOfCircle CenterX=0 CenterY=0 CenterZ=0 NormalX=0 NormalY=0 NormalZ=1 AngleXU=0 Radius=34.6079 StartAngle=5.41052 EndAngle=10.2974
    g2: LineSegment [constr] StartX=0 StartY=0 StartZ=0 EndX=-23.0169 EndY=-27.4304 EndZ=0
    g3: LineSegment [constr] StartX=0 StartY=0 StartZ=0 EndX=23.0169 EndY=-27.4304 EndZ=0
    g4: LineSegment StartX=22.2455 StartY=-26.5112 StartZ=0 EndX=23.0169 EndY=-27.4304 EndZ=0
    g5: LineSegment StartX=-23.0169 StartY=-27.4304 StartZ=0 EndX=-22.2455 EndY=-26.5112 EndZ=0
  constraints (16):
    c: Coincident(g0,g-1)
    c: PointOnObject(g0,g-3)
    c: Coincident(g1,g0)
    c: Coincident(g2,g0)
    c: Coincident(g2,g0)
    c: Coincident(g3,g0)
    c: Coincident(g3,g0)
    c: PointOnObject(g1,g3)
    c: PointOnObject(g1,g2)
    c: Distance(g0,g1) = 1.2
    c: Coincident(g4,g1)
    c: Coincident(g4,g0)
    c: Coincident(g5,g0)
    c: Coincident(g5,g1)
    c: Angle(g2,g-2) = 0.698132
    c: Angle(g-2,g3) = 0.698132
FEATURE [PartDesign::Pad] Pad071
  BaseFeature = -> Pad070
  Direction = (0,0,-1)
  Length = 11
  Length2 = 10
  Profile = -> Sketch182
  ReferenceAxis = -> Sketch182 [N_Axis]
  Refine = true
  Suppressed = false
  Type = 0
FEATURE [Sketcher::SketchObject] Sketch183
  ArcFitTolerance = 1e-06
  AttachmentSupport = -> [Pad071]
  FullyConstrained = false
  MakeInternals = false
  MapMode = 5
  Placement = pos=(0,0,-11) rot=(1,0,0;3.14159rad)
  sketch-geometry (5):
    g0: LineSegment StartX=-0.5 StartY=40.6798 StartZ=0 EndX=-0.5 EndY=28.3098 EndZ=0
    g1: LineSegment StartX=-0.5 StartY=28.3098 StartZ=0 EndX=0.5 EndY=28.3098 EndZ=0
    g2: LineSegment StartX=0.5 StartY=28.3098 StartZ=0 EndX=0.5 EndY=40.6798 EndZ=0
    g3: LineSegment StartX=0.5 StartY=40.6798 StartZ=0 EndX=-0.5 EndY=40.6798 EndZ=0
    g4: GeomPoint [constr] X=0 Y=34.4948 Z=0
  constraints (11):
    c: Coincident(g0,g1)
    c: Coincident(g1,g2)
    c: Coincident(g2,g3)
    c: Coincident(g3,g0)
    c: Vertical(g0)
    c: Vertical(g2)
    c: Horizontal(g1)
    c: Horizontal(g3)
    c: Symmetric(g2,g0,g4)
    c: PointOnObject(g4,g-2)
    c: DistanceX(g0,g2) = 1
FEATURE [PartDesign::Pocket] Pocket093
  BaseFeature = -> Pad071
  Direction = (0,0,1)
  Length = 6
  Length2 = 5
  Profile = -> Sketch183
  ReferenceAxis = -> Sketch183 [N_Axis]
  Refine = true
  Suppressed = false
  Type = 0
FEATURE [PartDesign::Fillet] Fillet044
  Base = -> Pocket093 [Edge2]
  BaseFeature = -> Pocket093
  Radius = 2
  Refine = true
  SupportTransform = false
  Suppressed = false
  UseAllEdges = false
FEATURE [PartDesign::Fillet] Fillet045
  Base = -> Fillet044 [Edge21]
  BaseFeature = -> Fillet044
  Radius = 1
  Refine = true
  SupportTransform = false
  Suppressed = false
  UseAllEdges = false
FEATURE [Sketcher::SketchObject] Sketch184
  ArcFitTolerance = 1e-06
  AttachmentSupport = -> [Fillet045]
  FullyConstrained = false
  MakeInternals = false
  MapMode = 5
  Placement = pos=(0,0,2) rot=(0,0,1;0rad)
  sketch-geometry (2):
    g0: Circle [constr] CenterX=0 CenterY=0 CenterZ=0 NormalX=0 NormalY=0 NormalZ=1 AngleXU=0 Radius=24.6129
    g1: Circle CenterX=-21.0901 CenterY=12.6886 CenterZ=0 NormalX=0 NormalY=0 NormalZ=1 AngleXU=0 Radius=6
  constraints (3):
    c: Coincident(g0,g-1)
    c: Diameter(g1) = 12
    c: PointOnObject(g1,g0)
FEATURE [PartDesign::Pocket] Pocket094
  BaseFeature = -> Fillet045
  Direction = (0,0,-1)
  Length = 5
  Length2 = 5
  Profile = -> Sketch184
  ReferenceAxis = -> Sketch184 [N_Axis]
  Refine = true
  Suppressed = false
  Type = 0
FEATURE [PartDesign::PolarPattern] PolarPattern
  Angle = 241
  Axis = -> Sketch184 [N_Axis]
  BaseFeature = -> Pocket094
  Mode = 0
  Occurrences = 5
  Offset = 120
  Originals = -> [Pocket094]
  Refine = true
  Suppressed = false
  TransformMode = 0
FEATURE [Sketcher::SketchObject] Sketch186
  ArcFitTolerance = 1e-06
  AttachmentSupport = -> [PolarPattern]
  FullyConstrained = false
  MakeInternals = false
  MapMode = 5
  Placement = pos=(0,0,2) rot=(0,0,1;0rad)
  sketch-geometry (4):
    g0: Circle CenterX=0 CenterY=14.5045 CenterZ=0 NormalX=0 NormalY=0 NormalZ=1 AngleXU=0 Radius=1.3
    g1: Circle CenterX=-9.41196 CenterY=-11.0361 CenterZ=0 NormalX=0 NormalY=0 NormalZ=1 AngleXU=0 Radius=1.3
    g2: Circle CenterX=9.41196 CenterY=-11.0361 CenterZ=0 NormalX=0 NormalY=0 NormalZ=1 AngleXU=0 Radius=1.3
    g3: Circle [constr] CenterX=0 CenterY=0 CenterZ=0 NormalX=0 NormalY=0 NormalZ=1 AngleXU=0 Radius=14.5045
  constraints (9):
    c: PointOnObject(g0,g-2)
    c: Coincident(g3,g-1)
    c: PointOnObject(g0,g3)
    c: PointOnObject(g2,g3)
    c: Horizontal(g1,g2)
    c: Equal(g1,g2)
    c: Equal(g1,g0)
    c: Diameter(g1) = 2.6
    c: PointOnObject(g1,g3)
FEATURE [PartDesign::Pocket] Pocket095
  BaseFeature = -> PolarPattern
  Direction = (0,0,-1)
  Length = 5
  Length2 = 5
  Profile = -> Sketch186
  ReferenceAxis = -> Sketch186 [N_Axis]
  Refine = true
  Suppressed = false
  Type = 0
FEATURE [PartDesign::Body] Body042  label="ENDSTOP WHEEL 2"
  AllowCompound = false
  Group = -> [Sketch181,Pad070,Sketch182,Pad071,Sketch183,Pocket093,Fillet044,Fillet045,Sketch184,Pocket094,PolarPattern,Sketch186,Pocket095]
  Origin = -> Origin062
  Placement = pos=(121.5,81,-43.5) rot=(1,0,0;3.14159rad)
  Tip = -> Pocket095
FEATURE [Part::Feature] Part__Feature059  label="Arm_elbow_plate_top_long"
  Placement = pos=(0,-0.2,21.6) rot=(0,0,1;0rad)
  shape: bbox 42 x 217.4 x 6 mm, 99 faces (baked)
FEATURE [Part::Feature] Part__Feature060  label="MG995"
  Placement = pos=(1.9e-14,159.4,18.9) rot=(0,0,-1;1.5708rad)
  shape: bbox 20 x 54.66 x 44.93 mm, 459 faces (baked)
FEATURE [Part::Feature] Part__Feature061  label="ROD 8X80"
  Placement = pos=(0,0,-1.6) rot=(0,0,1;0rad)
  shape: bbox 8 x 8 x 80 mm, 3 faces (baked)
FEATURE [Part::Feature] Part__Feature062  label="p  BEARING, METRIC 600 MINIATURE SERIES, DOUBLE-SEALED  8mm ID × 22 OD × 7 W  —  608-2RS002"
  Placement = pos=(0,169.9,1.8) rot=(0,0,1;0rad)
  shape: bbox 23.81 x 23.81 x 7.015 mm, 606 faces (baked)
FEATURE [Part::Feature] Part__Feature063  label="TIP HEAD"
  Placement = pos=(0,170,33.3) rot=(0,0,1;0rad)
  shape: bbox 48 x 70.02 x 35 mm, 10 faces (baked)
FEATURE [Part::Feature] Part__Feature064  label="Arm_elbow_plate_bot_long"
  Placement = pos=(0,-0.2,-0.8) rot=(0,0,1;0rad)
  shape: bbox 42 x 217.5 x 6 mm, 88 faces (baked)
FEATURE [Part::Feature] Part__Feature065  label="ELBOW RIGTH SIDE"
  shape: bbox 12 x 149.6 x 28 mm, 28 faces (baked)
FEATURE [Part::Feature] Part__Feature066  label="ELBOW SHOULDER END TIP001"
  Placement = pos=(1.49e-13,209.7,27.9) rot=(0,0,1;3.14159rad)
  shape: bbox 94 x 68.75 x 28 mm, 81 faces (baked)
FEATURE [Part::Feature] Part__Feature067  label="RODHUB2"
  Placement = pos=(0,0,-1) rot=(0,0,1;0rad)
  shape: bbox 25 x 24.98 x 39 mm, 30 faces (baked)
FEATURE [App::Part] ELBOW
  Group = -> [Part__Feature059,Part__Feature060,Part__Feature061,Part__Feature062,Part__Feature063,Part__Feature064,Part__Feature065,Part__Feature066,Part__Feature067]
  Origin = -> Origin063
  Placement = pos=(0,210.3,-58.6) rot=(0,0,1;0rad)
FEATURE [Part::Feature] Part__Feature068  label="Шкив GT2 60T b8 (6mm)"
  Placement = pos=(0,5.4e-15,24.6) rot=(-1,0,0;1.5708rad)
  shape: bbox 40 x 40 x 16 mm, 326 faces (baked)
FEATURE [Part::Feature] Part__Feature069  label="Шкив GT2 60T b8 (6mm)001"
  Placement = pos=(0,-1.4e-14,-16) rot=(-1,0,0;1.5708rad)
  shape: bbox 40 x 40 x 16 mm, 326 faces (baked)
FEATURE [Part::Feature] Part__Feature070  label="Arm_shoulder_Plate_Bottom"
  Placement = pos=(0,0,2.5) rot=(0,0,1;0rad)
  shape: bbox 46 x 252 x 7.293 mm, 112 faces (baked)
FEATURE [Part::Feature] Part__Feature071  label="ROD 8X40"
  Placement = pos=(0,3e-16,1.1) rot=(0,0,1;0rad)
  shape: bbox 8 x 8 x 40 mm, 3 faces (baked)
FEATURE [Part::Feature] Part__Feature072  label="ROD 8X60"
  Placement = pos=(0,0,1) rot=(1,0,0;3.14159rad)
  shape: bbox 8 x 8 x 60 mm, 3 faces (baked)
FEATURE [Part::Feature] Part__Feature073  label="bearing003"
  shape: bbox 8.659 x 4.3 x 8.659 mm, 17 faces (baked)
FEATURE [Part::Feature] Part__Feature074  label="bearing004"
  shape: bbox 8.659 x 4.3 x 8.659 mm, 17 faces (baked)
FEATURE [App::Part] bearing002  label="bearing005"
  Group = -> [Part__Feature073,Part__Feature074]
  Origin = -> Origin064
FEATURE [Part::Feature] Part__Feature075  label="outer_plate001"
  shape: bbox 12.9 x 8.6 x 12.9 mm, 12 faces (baked)
FEATURE [App::Part] GT2_Pulley_3mm_bore_v009  label="GT2 Pulley 3mm bore v009"
  Group = -> [bearing002,Part__Feature075]
  Origin = -> Origin065
  Placement = pos=(11.5,71.2,-4) rot=(-1,0,0;1.5708rad)
FEATURE [Part::Feature] Part__Feature076  label="M3x20-Screw"
  Placement = pos=(11.2,71.1,9) rot=(0,0,1;0rad)
  shape: bbox 5.953 x 5.953 x 22 mm, 19 faces (baked)
FEATURE [Part::Feature] Part__Feature077  label="M3x35-Screw"
  Placement = pos=(19.5,60,-22) rot=(1,0,0;3.14159rad)
  shape: bbox 5.953 x 5.953 x 37 mm, 19 faces (baked)
FEATURE [Part::Feature] Part__Feature078  label="M3x35-Screw016"
  Placement = pos=(18.5,160,-21.5) rot=(1,0,0;3.14159rad)
  shape: bbox 5.953 x 5.953 x 37 mm, 19 faces (baked)
FEATURE [Part::Feature] Part__Feature079  label="M3x35-Screw017"
  Placement = pos=(-19,60,-22) rot=(1,0,0;3.14159rad)
  shape: bbox 5.953 x 5.953 x 37 mm, 19 faces (baked)
FEATURE [Part::Feature] Part__Feature080  label="M3x35-Screw018"
  Placement = pos=(-18.5,160,-21.5) rot=(1,0,0;3.14159rad)
  shape: bbox 5.953 x 5.953 x 37 mm, 19 faces (baked)
FEATURE [Part::Feature] Part__Feature081  label="M3x10-Screw001"
  Placement = pos=(0,232.3,-20.5) rot=(-1,0,0;1.5708rad)
  shape: bbox 5.953 x 12 x 5.953 mm, 18 faces (baked)
FEATURE [Part::Feature] Part__Feature082  label="Arm_shoulder_Plate_Top"
  Placement = pos=(0,0,-21.5) rot=(0,0,1;0rad)
  shape: bbox 46 x 252 x 7.293 mm, 96 faces (baked)
FEATURE [Part::Feature] Part__Feature083  label="GT2_40T_8_6"
  Placement = pos=(0,0,-15) rot=(0,0,1;0rad)
  shape: bbox 30.31 x 30.31 x 15 mm, 348 faces (baked)
FEATURE [Part::Feature] Part__Feature084  label="GT2_40T_8_007"
  Placement = pos=(0,210,-15) rot=(0,0,1;0rad)
  shape: bbox 30.31 x 30.31 x 15 mm, 348 faces (baked)
FEATURE [Part::Feature] Part__Feature085  label="SHOULDER LEFT SIDE"
  Placement = pos=(19,0,-21.5) rot=(0,0,1;0rad)
  shape: bbox 9.892 x 189.9 x 30 mm, 30 faces (baked)
FEATURE [Part::Feature] Part__Feature086  label="SHOULDER RIGHT SIDE"
  Placement = pos=(-19,-8e-16,8.5) rot=(0,1,0;3.14159rad)
  shape: bbox 9.892 x 189.9 x 30 mm, 30 faces (baked)
FEATURE [Part::Feature] Part__Feature087  label="SHOULDER END Z AXIS"
  Placement = pos=(0,2.5,7.5) rot=(0,0,1;0rad)
  shape: bbox 55.39 x 39.3 x 30 mm, 66 faces (baked)
FEATURE [Part::Feature] Part__Feature088  label="SHOULDER END TIP"
  Placement = pos=(0,0.5,7.5) rot=(0,0,1;0rad)
  shape: bbox 52 x 39.5 x 30 mm, 70 faces (baked)
FEATURE [Part::Feature] Part__Feature089  label="Board^Optical Endstop Switch"
  shape: bbox 33 x 1.612 x 10 mm, 109 faces (baked)
FEATURE [Part::Feature] Part__Feature090  label="TCST2103^Optical Endstop Switch"
  Placement = pos=(-0.05,1.6,-8.15) rot=(0,0,1;0rad)
  shape: bbox 24.75 x 13.8 x 6.711 mm, 252 faces (baked)
FEATURE [Part::Feature] Part__Feature091  label="RES_0805^Optical Endstop Switch"
  Placement = pos=(25.5,1.6,-1.86) rot=(0,0,1;0rad)
  shape: bbox 0.5 x 0.45 x 1.2 mm, 18 faces (baked)
FEATURE [Part::Feature] Part__Feature092  label="RES_0805^Optical Endstop Switch001"
  Placement = pos=(25.5,1.6,-1.86) rot=(0,0,1;0rad)
  shape: bbox 0.5 x 0.45 x 1.2 mm, 18 faces (baked)
FEATURE [Part::Feature] Part__Feature093  label="RES_0805^Optical Endstop Switch002"
  Placement = pos=(25.5,1.6,-1.86) rot=(0,0,1;0rad)
  shape: bbox 1.001 x 0.4812 x 1.201 mm, 64 faces (baked)
FEATURE [App::Part] RES_0805_Optical_Endstop_Switch003  label="RES_0805^Optical Endstop Switch003"
  Group = -> [Part__Feature091,Part__Feature092,Part__Feature093]
  Origin = -> Origin066
FEATURE [Part::Feature] Part__Feature094  label="RES_0805^Optical Endstop Switch004"
  Placement = pos=(13.25,0,-2.2) rot=(0,0,1;3.14159rad)
  shape: bbox 0.5 x 0.45 x 1.2 mm, 18 faces (baked)
FEATURE [Part::Feature] Part__Feature095  label="RES_0805^Optical Endstop Switch005"
  Placement = pos=(13.25,0,-2.2) rot=(0,0,1;3.14159rad)
  shape: bbox 0.5 x 0.45 x 1.2 mm, 18 faces (baked)
FEATURE [Part::Feature] Part__Feature096  label="RES_0805^Optical Endstop Switch006"
  Placement = pos=(13.25,0,-2.2) rot=(0,0,1;3.14159rad)
  shape: bbox 1.001 x 0.4812 x 1.201 mm, 64 faces (baked)
FEATURE [App::Part] RES_0805_Optical_Endstop_Switch007  label="RES_0805^Optical Endstop Switch007"
  Group = -> [Part__Feature094,Part__Feature095,Part__Feature096]
  Origin = -> Origin067
FEATURE [Part::Feature] Part__Feature097  label="LED_0805_Green^Optical Endstop Switch"
  Placement = pos=(27.5,1.6,-5.625) rot=(0,1,0;3.14159rad)
  shape: bbox 1 x 0.28 x 1.25 mm, 6 faces (baked)
FEATURE [Part::Feature] Part__Feature098  label="LED_0805_Green^Optical Endstop Switch001"
  Placement = pos=(27.5,1.6,-5.625) rot=(0,1,0;3.14159rad)
  shape: bbox 0.4 x 0.28 x 1.25 mm, 8 faces (baked)
FEATURE [Part::Feature] Part__Feature099  label="LED_0805_Green^Optical Endstop Switch002"
  Placement = pos=(27.5,1.6,-5.625) rot=(0,1,0;3.14159rad)
  shape: bbox 0.4 x 0.28 x 1.25 mm, 8 faces (baked)
FEATURE [Part::Feature] Part__Feature100  label="LED_0805_Green^Optical Endstop Switch003"
  Placement = pos=(27.5,1.6,-5.625) rot=(0,1,0;3.14159rad)
  shape: bbox 1 x 0.4049 x 1.25 mm, 18 faces (baked)
FEATURE [App::Part] LED_0805_Green_Optical_Endstop_Switch004  label="LED_0805_Green^Optical Endstop Switch004"
  Group = -> [Part__Feature097,Part__Feature098,Part__Feature099,Part__Feature100]
  Origin = -> Origin068
FEATURE [Part::Feature] Part__Feature101  label="RES_0805^Optical Endstop Switch008"
  Placement = pos=(13.25,0,-6.6) rot=(0,0,1;3.14159rad)
  shape: bbox 0.5 x 0.45 x 1.2 mm, 18 faces (baked)
FEATURE [Part::Feature] Part__Feature102  label="RES_0805^Optical Endstop Switch009"
  Placement = pos=(13.25,0,-6.6) rot=(0,0,1;3.14159rad)
  shape: bbox 0.5 x 0.45 x 1.2 mm, 18 faces (baked)
FEATURE [Part::Feature] Part__Feature103  label="RES_0805^Optical Endstop Switch010"
  Placement = pos=(13.25,0,-6.6) rot=(0,0,1;3.14159rad)
  shape: bbox 1.001 x 0.4812 x 1.201 mm, 64 faces (baked)
FEATURE [App::Part] RES_0805_Optical_Endstop_Switch011  label="RES_0805^Optical Endstop Switch011"
  Group = -> [Part__Feature101,Part__Feature102,Part__Feature103]
  Origin = -> Origin069
FEATURE [Part::Feature] Part__Feature104  label="JST-XH-3A^Optical Endstop Switch"
  Placement = pos=(32.67,0,-9.95) rot=(0.707107,0,0.707107;3.14159rad)
  shape: bbox 5.75 x 10.5 x 9.9 mm, 107 faces (baked)
FEATURE [App::Part] Optical_Endstop_Switch  label="Optical Endstop Switch"
  Group = -> [Part__Feature089,Part__Feature090,RES_0805_Optical_Endstop_Switch003,RES_0805_Optical_Endstop_Switch007,LED_0805_Green_Optical_Endstop_Switch004,RES_0805_Optical_Endstop_Switch011,Part__Feature104]
  Origin = -> Origin070
  Placement = pos=(-5,176.8,12.9) rot=(0.57735,-0.57735,-0.57735;2.0944rad)
FEATURE [Part::Feature] Part__Feature105  label="Board^Optical Endstop Switch001"
  shape: bbox 33 x 1.612 x 10 mm, 109 faces (baked)
FEATURE [Part::Feature] Part__Feature106  label="TCST2103^Optical Endstop Switch001"
  Placement = pos=(-0.05,1.6,-8.15) rot=(0,0,1;0rad)
  shape: bbox 24.75 x 13.8 x 6.711 mm, 252 faces (baked)
FEATURE [Part::Feature] Part__Feature107  label="RES_0805^Optical Endstop Switch012"
  Placement = pos=(25.5,1.6,-1.86) rot=(0,0,1;0rad)
  shape: bbox 0.5 x 0.45 x 1.2 mm, 18 faces (baked)
FEATURE [Part::Feature] Part__Feature108  label="RES_0805^Optical Endstop Switch013"
  Placement = pos=(25.5,1.6,-1.86) rot=(0,0,1;0rad)
  shape: bbox 0.5 x 0.45 x 1.2 mm, 18 faces (baked)
FEATURE [Part::Feature] Part__Feature109  label="RES_0805^Optical Endstop Switch014"
  Placement = pos=(25.5,1.6,-1.86) rot=(0,0,1;0rad)
  shape: bbox 1.001 x 0.4812 x 1.201 mm, 64 faces (baked)
FEATURE [App::Part] RES_0805_Optical_Endstop_Switch021  label="RES_0805^Optical Endstop Switch021"
  Group = -> [Part__Feature107,Part__Feature108,Part__Feature109]
  Origin = -> Origin071
FEATURE [Part::Feature] Part__Feature110  label="RES_0805^Optical Endstop Switch015"
  Placement = pos=(13.25,0,-2.2) rot=(0,0,1;3.14159rad)
  shape: bbox 0.5 x 0.45 x 1.2 mm, 18 faces (baked)
FEATURE [Part::Feature] Part__Feature111  label="RES_0805^Optical Endstop Switch016"
  Placement = pos=(13.25,0,-2.2) rot=(0,0,1;3.14159rad)
  shape: bbox 0.5 x 0.45 x 1.2 mm, 18 faces (baked)
FEATURE [Part::Feature] Part__Feature112  label="RES_0805^Optical Endstop Switch017"
  Placement = pos=(13.25,0,-2.2) rot=(0,0,1;3.14159rad)
  shape: bbox 1.001 x 0.4812 x 1.201 mm, 64 faces (baked)
FEATURE [App::Part] RES_0805_Optical_Endstop_Switch022  label="RES_0805^Optical Endstop Switch022"
  Group = -> [Part__Feature110,Part__Feature111,Part__Feature112]
  Origin = -> Origin072
FEATURE [Part::Feature] Part__Feature113  label="LED_0805_Green^Optical Endstop Switch006"
  Placement = pos=(27.5,1.6,-5.625) rot=(0,1,0;3.14159rad)
  shape: bbox 1 x 0.28 x 1.25 mm, 6 faces (baked)
FEATURE [Part::Feature] Part__Feature114  label="LED_0805_Green^Optical Endstop Switch007"
  Placement = pos=(27.5,1.6,-5.625) rot=(0,1,0;3.14159rad)
  shape: bbox 0.4 x 0.28 x 1.25 mm, 8 faces (baked)
FEATURE [Part::Feature] Part__Feature115  label="LED_0805_Green^Optical Endstop Switch008"
  Placement = pos=(27.5,1.6,-5.625) rot=(0,1,0;3.14159rad)
  shape: bbox 0.4 x 0.28 x 1.25 mm, 8 faces (baked)
FEATURE [Part::Feature] Part__Feature116  label="LED_0805_Green^Optical Endstop Switch009"
  Placement = pos=(27.5,1.6,-5.625) rot=(0,1,0;3.14159rad)
  shape: bbox 1 x 0.4049 x 1.25 mm, 18 faces (baked)
FEATURE [App::Part] LED_0805_Green_Optical_Endstop_Switch005  label="LED_0805_Green^Optical Endstop Switch005"
  Group = -> [Part__Feature113,Part__Feature114,Part__Feature115,Part__Feature116]
  Origin = -> Origin073
FEATURE [Part::Feature] Part__Feature117  label="RES_0805^Optical Endstop Switch018"
  Placement = pos=(13.25,0,-6.6) rot=(0,0,1;3.14159rad)
  shape: bbox 0.5 x 0.45 x 1.2 mm, 18 faces (baked)
FEATURE [Part::Feature] Part__Feature118  label="RES_0805^Optical Endstop Switch019"
  Placement = pos=(13.25,0,-6.6) rot=(0,0,1;3.14159rad)
  shape: bbox 0.5 x 0.45 x 1.2 mm, 18 faces (baked)
FEATURE [Part::Feature] Part__Feature119  label="RES_0805^Optical Endstop Switch020"
  Placement = pos=(13.25,0,-6.6) rot=(0,0,1;3.14159rad)
  shape: bbox 1.001 x 0.4812 x 1.201 mm, 64 faces (baked)
FEATURE [App::Part] RES_0805_Optical_Endstop_Switch023  label="RES_0805^Optical Endstop Switch023"
  Group = -> [Part__Feature117,Part__Feature118,Part__Feature119]
  Origin = -> Origin074
FEATURE [Part::Feature] Part__Feature120  label="JST-XH-3A^Optical Endstop Switch001"
  Placement = pos=(32.67,0,-9.95) rot=(0.707107,0,0.707107;3.14159rad)
  shape: bbox 5.75 x 10.5 x 9.9 mm, 107 faces (baked)
FEATURE [App::Part] Optical_Endstop_Switch001  label="Optical Endstop Switch001"
  Group = -> [Part__Feature105,Part__Feature106,RES_0805_Optical_Endstop_Switch021,RES_0805_Optical_Endstop_Switch022,LED_0805_Green_Optical_Endstop_Switch005,RES_0805_Optical_Endstop_Switch023,Part__Feature120]
  Origin = -> Origin075
  Placement = pos=(5,22.8,12.9) rot=(0.57735,0.57735,0.57735;2.0944rad)
FEATURE [Part::Feature] Part__Feature121  label="ENDSTOP SUPPORT"
  Placement = pos=(7e-15,174,8.5) rot=(0,0,1;3.14159rad)
  shape: bbox 16.22 x 34.55 x 4.5 mm, 22 faces (baked)
FEATURE [Part::Feature] Part__Feature122  label="ENDSTOP SUPPORT001"
  Placement = pos=(3e-15,25.5,8.5) rot=(0,0,1;0rad)
  shape: bbox 16.22 x 34.55 x 4.5 mm, 22 faces (baked)
FEATURE [App::Part] SHOULDER
  Group = -> [Part__Feature068,Part__Feature069,Part__Feature070,Part__Feature071,Part__Feature072,GT2_Pulley_3mm_bore_v009,Part__Feature076,Part__Feature077,Part__Feature078,Part__Feature079,Part__Feature080,Part__Feature081,Part__Feature082,Part__Feature083,Part__Feature084,Part__Feature085,Part__Feature086,Part__Feature087,Part__Feature088,Optical_Endstop_Switch,Optical_Endstop_Switch001,Part__Feature121,+1 more]
  Origin = -> Origin076
  Placement = pos=(1.7e-15,0,-14) rot=(0,1,0;3.14159rad)
FEATURE [Part::Feature] Part__Feature123  label="EJE"
  Placement = pos=(3e-15,-0.2,-54.6) rot=(0,1,0;3.14159rad)
  shape: bbox 27.48 x 30 x 179 mm, 32 faces (baked)
FEATURE [Part::Feature] Part__Feature124  label="COLAR"
  Placement = pos=(0,0,-33.2) rot=(0,0,1;0rad)
  shape: bbox 12 x 12 x 8 mm, 4 faces (baked)
FEATURE [App::Part] CUTIING_HEAD  label="CUTIING HEAD"
  Group = -> [Part__Feature123,Part__Feature124]
  Origin = -> Origin077
  Placement = pos=(0,379.4,-7.3) rot=(0,0,1;0rad)
FEATURE [App::Part] ARM_Long
  Group = -> [ELBOW,SHOULDER,CUTIING_HEAD]
  Origin = -> Origin078
  Placement = pos=(-0.5,83,-3.5) rot=(0,0,1;0rad)
FEATURE [Mesh::Feature] Mesh  label="PLATES SPACER (Meshed)"
FEATURE [Sketcher::SketchObject] Sketch187
  ArcFitTolerance = 1e-06
  AttachmentSupport = -> [Pocket004]
  ExternalGeometry = -> [Pocket004]
  FullyConstrained = false
  MakeInternals = false
  MapMode = 5
  Placement = pos=(0,0,0) rot=(1,0,0;3.14159rad)
  sketch-geometry (16):
    g0: ArcOfCircle [constr] CenterX=0 CenterY=-43 CenterZ=0 NormalX=0 NormalY=0 NormalZ=1 AngleXU=0 Radius=34.5224 StartAngle=4.71239 EndAngle=6.28319
    g1: ArcOfCircle CenterX=0 CenterY=-43 CenterZ=0 NormalX=0 NormalY=0 NormalZ=1 AngleXU=0 Radius=38.0548 StartAngle=6.04392 EndAngle=6.28319
    g2: ArcOfCircle CenterX=34.5224 CenterY=-43 CenterZ=0 NormalX=0 NormalY=0 NormalZ=1 AngleXU=0 Radius=3.53234 StartAngle=4e-16 EndAngle=1.5708
    g3: LineSegment StartX=34.5224 StartY=-39.4677 StartZ=0 EndX=18.3596 EndY=-39.4677 EndZ=0
    g4: LineSegment [constr] StartX=0 StartY=-43 StartZ=0 EndX=58.8301 EndY=-43 EndZ=0
    g5: LineSegment [constr] StartX=-10.1518 StartY=0 StartZ=0 EndX=17.2743 EndY=0 EndZ=0
    g6: LineSegment [constr] StartX=-14.0619 StartY=-32 StartZ=0 EndX=-14.0619 EndY=-54 EndZ=0
    g7: LineSegment [constr] StartX=-14.0619 StartY=-54 StartZ=0 EndX=12.8886 EndY=-54 EndZ=0
    g8: LineSegment [constr] StartX=12.8886 StartY=-54 StartZ=0 EndX=12.8886 EndY=-32 EndZ=0
    g9: LineSegment [constr] StartX=12.8886 StartY=-32 StartZ=0 EndX=-14.0619 EndY=-32 EndZ=0
    g10: Circle CenterX=34.5224 CenterY=-43 CenterZ=0 NormalX=0 NormalY=0 NormalZ=1 AngleXU=0 Radius=0.75
    g11: Circle CenterX=34.4362 CenterY=-45.438 CenterZ=0 NormalX=0 NormalY=0 NormalZ=1 AngleXU=0 Radius=0.75
    g12: Circle CenterX=34.1789 CenterY=-47.858 CenterZ=0 NormalX=0 NormalY=0 NormalZ=1 AngleXU=0 Radius=0.75
    g13: LineSegment StartX=13.5019 StartY=-55.9081 StartZ=0 EndX=32.0184 EndY=-55.9081 EndZ=0
    g14: ArcOfCircle CenterX=32.0184 CenterY=-50.8106 CenterZ=0 NormalX=0 NormalY=0 NormalZ=1 AngleXU=0 Radius=5.09743 StartAngle=4.71239 EndAngle=6.04392
    g15: LineSegment StartX=18.3596 StartY=-39.4677 StartZ=0 EndX=13.5019 EndY=-55.9081 EndZ=0
  constraints (32):
    c: Block(g0)
    c: Coincident(g0,g2)
    c: Coincident(g3,g2)
    c: Coincident(g-4,g3)
    c: Horizontal(g4)
    c: Tangent(g5,g-1)
    c: Coincident(g6,g7)
    c: Coincident(g7,g8)
    c: Coincident(g8,g9)
    c: Coincident(g9,g6)
    c: Vertical(g6)
    c: Horizontal(g7)
    c: Horizontal(g9)
    c: Tangent(g9,g-5)
    c: Symmetric(g7,g8,g4)
    c: Horizontal(g3)
    c: Tangent(g2,g1) = -1.5708
    c: Coincident(g1,g4)
    c: Coincident(g0,g1)
    c: Coincident(g10,g0)
    c: PointOnObject(g11,g0)
    c: PointOnObject(g12,g0)
    c: Equal(g10,g11)
    c: Equal(g10,g12)
    c: Diameter(g10) = 1.5
    c: PointOnObject(g13,g-6)
    c: PointOnObject(g13,g0)
    c: Tangent(g14,g13) = -1.5708
    c: Tangent(g1,g14) = -1.5708
    c: Coincident(g15,g3)
    c: Coincident(g15,g13)
    c: Horizontal(g13)
FEATURE [PartDesign::Pad] Pad072
  BaseFeature = -> Pocket004
  Direction = (0,0,-1)
  Length = 6
  Length2 = 10
  Profile = -> Sketch187
  ReferenceAxis = -> Sketch187 [N_Axis]
  Refine = true
  Reversed = true
  Suppressed = false
  Type = 0
FEATURE [PartDesign::Body] Body019  label="ARM SHOULDER CONNECTOR ALUMINIUM"
  AllowCompound = false
  Group = -> [Sketch022,Pad018,Sketch004,Pocket002,Sketch024,Pocket003,Sketch025,Pocket004,Sketch187,Pad072]
  Origin = -> Origin044
  Placement = pos=(70.6,154.5,-60) rot=(0,0,1;0rad)
  Tip = -> Pad072
FEATURE [PartDesign::FeatureBase] Clone001
  BaseFeature = -> Body019
  Placement = pos=(0,39.8,-51) rot=(0,0,1;0rad)
  Suppressed = false
FEATURE [PartDesign::Body] Body022  label="Body"
  AllowCompound = false
  Group = -> [Clone001]
  Origin = -> Origin047
  Placement = pos=(1.27e-14,0,-27.3) rot=(0,1,0;3.14159rad)
  Tip = -> Clone001
FEATURE [App::Part] Part016  label="ARM SHOULDER CONNECTOR 1"
  Group = -> [Part__Feature052,Body019,Body023]
  Origin = -> Origin050
  Placement = pos=(0,0,9.4) rot=(0,0,1;0rad)
FEATURE [App::Part] Part  label="ZAXIS-FULL ASSY"
  Group = -> [Part015,Body020,Part__Feature,Body021,Part__Feature001,Part__Feature050,Part__Feature051,Body022,GT2_Pulley_Assembly_With_Grub_Screws,GT2_Pulley_Assembly_With_Grub_Screws001,Part016,Body026,Body027,Body028,ARM_Long,Body042,Part__Feature008,Part__Feature003,p__BEARING__SINGLE_ROW_RADIAL__DOUBLE_SHIELDED__METRIC_6000_ZZ_SERIES_______6002_ZZ_____15mm_ID____32mm_OD____9mm_W,+3 more]
  Origin = -> Origin
  Placement = pos=(0,-2.5,95.6) rot=(0,0,1;0rad)
FEATURE [App::Part] Part001  label="ZAXIS FULL ASSEMBLE"
  Group = -> [Arm_Base_MotorPlate_1_1_003,Arm_Shoulder_Connector_1_1_003,Arm_Base_ZHub_Bottom_1_0_0,Arm_Base_ZHub_Top_1_0_0,Arm_Shoulder_Connector_1_1_2,Part__Feature009,GT2_20_T_5mm_bore,GT2_20_T_5mm_bore001,Part002,Part]
  Origin = -> Origin002
FEATURE [Mesh::Feature] Mesh002  label="ARM SHOULDER CONNECTOR ALUMINIUM (Meshed)"
